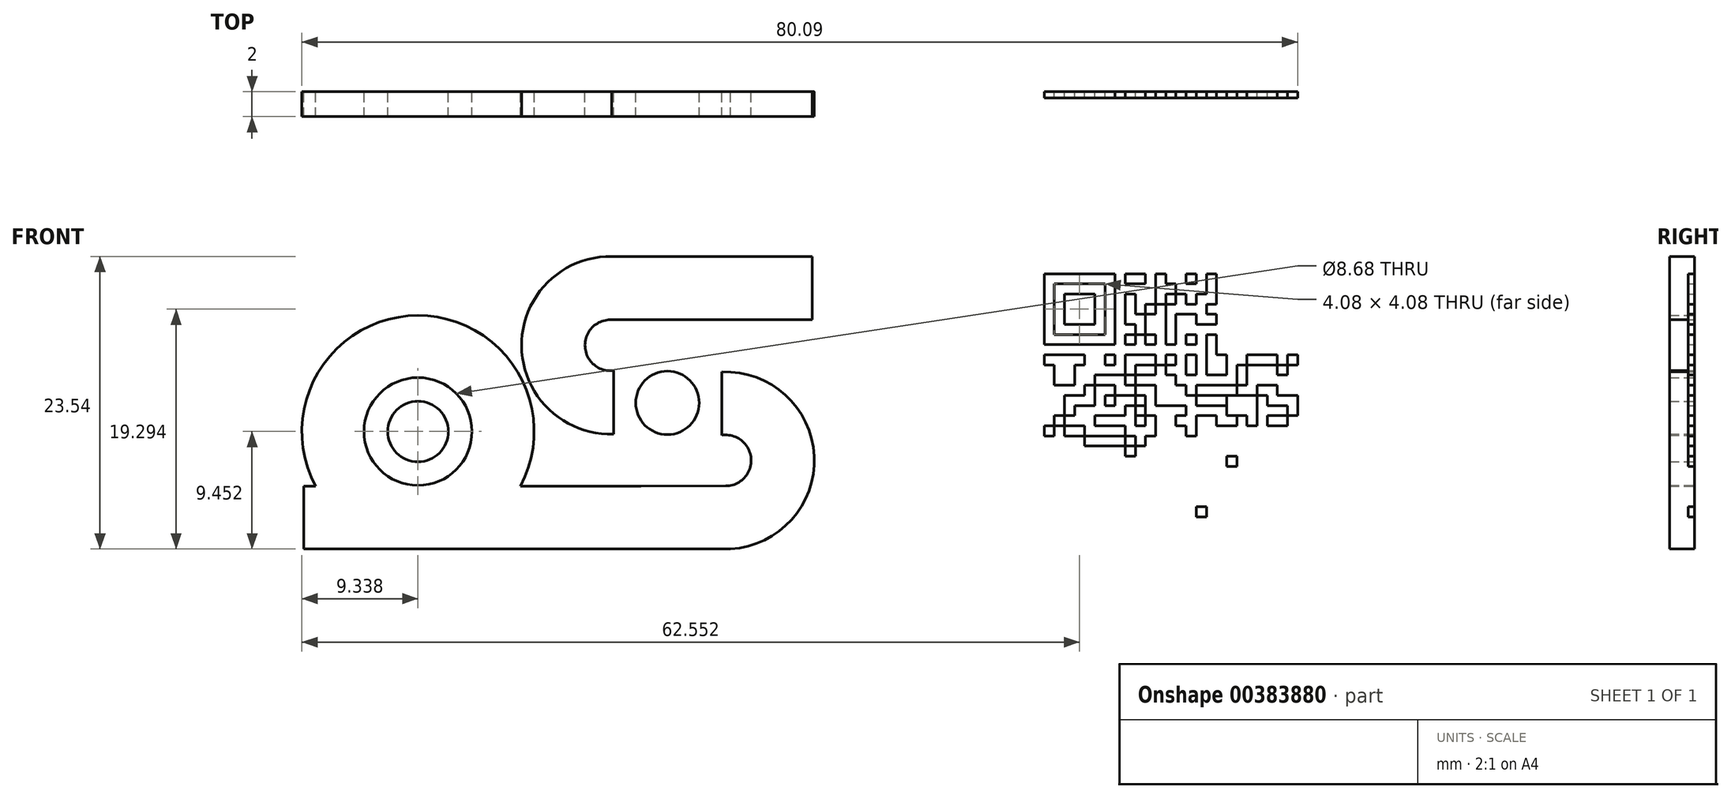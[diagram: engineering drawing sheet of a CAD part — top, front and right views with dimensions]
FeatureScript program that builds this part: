
annotation { "Feature Type Name" : "Feature", "Feature Type Description" : "" }
export const myFeature = defineFeature(function(context is Context, id is Id, definition is map)
    precondition{}
    {
        {
            var Q0;
            Q0=qCreatedBy(makeId("Front.planeOp"),FACE);
            var sketch = newSketch(context, id + "F0", { "sketchPlane" : qUnion([Q0])});
            skCircle(sketch, "E0", {"center": v(-32.73, 10.63) * mm, "radius": 2.44 * mm});
            skCircle(sketch, "E1.0", {"center": v(-32.73, 10.63) * mm, "radius": 4.34 * mm});
            skArc(sketch, "E2.0", {"start": v(-24.49, 6.24) * mm, "mid": v(-32.74, 19.97) * mm, "end": v(-40.97, 6.22) * mm});
            skLineSegment(sketch, "E3", {"start": v(-40.97, 6.22) * mm, "end": v(-41.91, 6.22) * mm});
            skLineSegment(sketch, "E4", {"start": v(-41.91, 6.22) * mm, "end": v(-41.91, 1.18) * mm});
            skLineSegment(sketch, "E5", {"start": v(-41.91, 1.18) * mm, "end": v(-7.6, 1.18) * mm});
            skArc(sketch, "E6", {"start": v(-7.98, 6.25) * mm, "mid": v(-5.94, 8.46) * mm, "end": v(-8.3, 10.33) * mm});
            skCircle(sketch, "E7", {"center": v(-12.67, 12.94) * mm, "radius": 2.55 * mm});
            skLineSegment(sketch, "E8", {"start": v(-8.3, 10.33) * mm, "end": v(-8.3, 15.43) * mm});
            skArc(sketch, "E9.0", {"start": v(-8.37, 1.18) * mm, "mid": v(-0.86, 8.27) * mm, "end": v(-8.3, 15.43) * mm});
            skLineSegment(sketch, "E10", {"start": v(-24.49, 6.24) * mm, "end": v(-14.81, 6.24) * mm});
            skLineSegment(sketch, "E11", {"start": v(-14.81, 6.24) * mm, "end": v(-7.98, 6.25) * mm});
            skArc(sketch, "E12", {"start": v(-17.25, 19.62) * mm, "mid": v(-19.3, 17.45) * mm, "end": v(-17, 15.54) * mm});
            skArc(sketch, "E13.0", {"start": v(-17.16, 24.72) * mm, "mid": v(-24.4, 17.5) * mm, "end": v(-17, 10.43) * mm});
            skLineSegment(sketch, "E14", {"start": v(-17, 15.54) * mm, "end": v(-17, 10.43) * mm});
            skLineSegment(sketch, "E15", {"start": v(-17.16, 24.72) * mm, "end": v(-1.01, 24.72) * mm});
            skLineSegment(sketch, "E16", {"start": v(-1.01, 24.72) * mm, "end": v(-1.01, 19.62) * mm});
            skLineSegment(sketch, "E17", {"start": v(-1.01, 19.62) * mm, "end": v(-17.25, 19.62) * mm});
            skSolve(sketch);
        }
        {
            var Q0;
            Q0=makeQuery(id+"F0.imprint","IMPRINT",FACE,{"disambiguationData":[TD([[makeQuery(id+"F0.imprint","IMPRINT",EDGE,{"derivedFrom":sQuery(id+"F0.wireOp",EDGE,"E1.0")}),-1.0]])]});
            var Q1;
            Q1=makeQuery(id+"F0.imprint","IMPRINT",FACE,{"disambiguationData":[TD([[makeQuery(id+"F0.imprint","IMPRINT",EDGE,{"derivedFrom":sQuery(id+"F0.wireOp",EDGE,"E0")}),1.0]])]});
            var Q2;
            Q2=makeQuery(id+"F0.imprint","IMPRINT",FACE,{"disambiguationData":[TD([[makeQuery(id+"F0.imprint","IMPRINT",EDGE,{"derivedFrom":sQuery(id+"F0.wireOp",EDGE,"E12")}),-1.0]])]});
            var Q3;
            Q3=makeQuery(id+"F0.imprint","IMPRINT",FACE,{"disambiguationData":[TD([[makeQuery(id+"F0.imprint","IMPRINT",EDGE,{"derivedFrom":sQuery(id+"F0.wireOp",EDGE,"E7")}),1.0]])]});
            extrude(context, id + "F1", {"entities" : qUnion([Q0, Q1, Q2, Q3]), "depth" : 2 * mm});
        }
        {
            var Q0;
            Q0=qCreatedBy(makeId("Front.planeOp"),FACE);
            var sketch = newSketch(context, id + "F2", { "sketchPlane" : qUnion([Q0])});
            skLineSegment(sketch, "E18", {"start": v(79.5, 79.25) * mm, "end": v(79.5, -80.75) * mm});
            skLineSegment(sketch, "E19", {"start": v(79.5, -80.75) * mm, "end": v(-80.5, -80.75) * mm});
            skLineSegment(sketch, "E20", {"start": v(80.5, 80.75) * mm, "end": v(80.5, -79.25) * mm});
            skLineSegment(sketch, "E21", {"start": v(80.5, -79.25) * mm, "end": v(-79.5, -79.25) * mm});
            skLineSegment(sketch, "E22", {"start": v(17.63, 23.33) * mm, "end": v(17.63, 22.51) * mm});
            skLineSegment(sketch, "E23", {"start": v(17.63, 22.51) * mm, "end": v(17.63, 21.7) * mm});
            skLineSegment(sketch, "E24", {"start": v(17.63, 21.7) * mm, "end": v(17.63, 20.88) * mm});
            skLineSegment(sketch, "E25", {"start": v(17.63, 20.88) * mm, "end": v(17.63, 20.07) * mm});
            skLineSegment(sketch, "E26", {"start": v(17.63, 20.07) * mm, "end": v(17.63, 19.25) * mm});
            skLineSegment(sketch, "E27", {"start": v(17.63, 19.25) * mm, "end": v(17.63, 18.44) * mm});
            skLineSegment(sketch, "E28", {"start": v(17.63, 18.44) * mm, "end": v(17.63, 17.62) * mm});
            skLineSegment(sketch, "E29", {"start": v(17.63, 17.62) * mm, "end": v(18.44, 17.62) * mm});
            skLineSegment(sketch, "E30", {"start": v(18.44, 17.62) * mm, "end": v(19.26, 17.62) * mm});
            skLineSegment(sketch, "E31", {"start": v(19.26, 17.62) * mm, "end": v(20.07, 17.62) * mm});
            skLineSegment(sketch, "E32", {"start": v(20.07, 17.62) * mm, "end": v(20.9, 17.62) * mm});
            skLineSegment(sketch, "E33", {"start": v(20.9, 17.62) * mm, "end": v(21.7, 17.62) * mm});
            skLineSegment(sketch, "E34", {"start": v(21.7, 17.62) * mm, "end": v(22.52, 17.62) * mm});
            skLineSegment(sketch, "E35", {"start": v(22.52, 17.62) * mm, "end": v(23.34, 17.62) * mm});
            skLineSegment(sketch, "E36", {"start": v(23.34, 17.62) * mm, "end": v(23.34, 18.44) * mm});
            skLineSegment(sketch, "E37", {"start": v(23.34, 18.44) * mm, "end": v(23.34, 19.25) * mm});
            skLineSegment(sketch, "E38", {"start": v(23.34, 19.25) * mm, "end": v(23.34, 20.07) * mm});
            skLineSegment(sketch, "E39", {"start": v(23.34, 20.07) * mm, "end": v(23.34, 20.88) * mm});
            skLineSegment(sketch, "E40", {"start": v(23.34, 20.88) * mm, "end": v(23.34, 21.7) * mm});
            skLineSegment(sketch, "E41", {"start": v(23.34, 21.7) * mm, "end": v(23.34, 22.51) * mm});
            skLineSegment(sketch, "E42", {"start": v(23.34, 22.51) * mm, "end": v(23.34, 23.33) * mm});
            skLineSegment(sketch, "E43", {"start": v(23.34, 23.33) * mm, "end": v(22.52, 23.33) * mm});
            skLineSegment(sketch, "E44", {"start": v(22.52, 23.33) * mm, "end": v(21.7, 23.33) * mm});
            skLineSegment(sketch, "E45", {"start": v(21.7, 23.33) * mm, "end": v(20.9, 23.33) * mm});
            skLineSegment(sketch, "E46", {"start": v(20.9, 23.33) * mm, "end": v(20.07, 23.33) * mm});
            skLineSegment(sketch, "E47", {"start": v(20.07, 23.33) * mm, "end": v(19.26, 23.33) * mm});
            skLineSegment(sketch, "E48", {"start": v(19.26, 23.33) * mm, "end": v(18.44, 23.33) * mm});
            skLineSegment(sketch, "E49", {"start": v(18.44, 23.33) * mm, "end": v(17.63, 23.33) * mm});
            skLineSegment(sketch, "E50", {"start": v(24.15, 23.33) * mm, "end": v(24.15, 22.51) * mm});
            skLineSegment(sketch, "E51", {"start": v(24.15, 22.51) * mm, "end": v(24.97, 22.51) * mm});
            skLineSegment(sketch, "E52", {"start": v(24.97, 22.51) * mm, "end": v(25.78, 22.51) * mm});
            skLineSegment(sketch, "E53", {"start": v(25.78, 22.51) * mm, "end": v(25.78, 23.33) * mm});
            skLineSegment(sketch, "E54", {"start": v(25.78, 23.33) * mm, "end": v(24.97, 23.33) * mm});
            skLineSegment(sketch, "E55", {"start": v(24.97, 23.33) * mm, "end": v(24.15, 23.33) * mm});
            skLineSegment(sketch, "E56", {"start": v(26.6, 23.33) * mm, "end": v(26.6, 22.51) * mm});
            skLineSegment(sketch, "E57", {"start": v(26.6, 22.51) * mm, "end": v(26.6, 21.7) * mm});
            skLineSegment(sketch, "E58", {"start": v(26.6, 21.7) * mm, "end": v(26.6, 20.88) * mm});
            skLineSegment(sketch, "E59", {"start": v(26.6, 20.88) * mm, "end": v(27.42, 20.88) * mm});
            skLineSegment(sketch, "E60", {"start": v(27.42, 20.88) * mm, "end": v(27.42, 21.7) * mm});
            skLineSegment(sketch, "E61", {"start": v(27.42, 21.7) * mm, "end": v(28.23, 21.7) * mm});
            skLineSegment(sketch, "E62", {"start": v(28.23, 21.7) * mm, "end": v(28.23, 22.51) * mm});
            skLineSegment(sketch, "E63", {"start": v(28.23, 22.51) * mm, "end": v(27.42, 22.51) * mm});
            skLineSegment(sketch, "E64", {"start": v(27.42, 22.51) * mm, "end": v(27.42, 23.33) * mm});
            skLineSegment(sketch, "E65", {"start": v(27.42, 23.33) * mm, "end": v(26.6, 23.33) * mm});
            skLineSegment(sketch, "E66", {"start": v(28.23, 21.7) * mm, "end": v(28.23, 20.88) * mm});
            skLineSegment(sketch, "E67", {"start": v(28.23, 20.88) * mm, "end": v(27.42, 20.88) * mm});
            skLineSegment(sketch, "E68", {"start": v(27.42, 20.88) * mm, "end": v(27.42, 20.07) * mm});
            skLineSegment(sketch, "E69", {"start": v(27.42, 20.07) * mm, "end": v(27.42, 19.25) * mm});
            skLineSegment(sketch, "E70", {"start": v(27.42, 19.25) * mm, "end": v(27.42, 18.44) * mm});
            skLineSegment(sketch, "E71", {"start": v(27.42, 18.44) * mm, "end": v(27.42, 17.62) * mm});
            skLineSegment(sketch, "E72", {"start": v(27.42, 17.62) * mm, "end": v(28.23, 17.62) * mm});
            skLineSegment(sketch, "E73", {"start": v(28.23, 17.62) * mm, "end": v(28.23, 18.44) * mm});
            skLineSegment(sketch, "E74", {"start": v(28.23, 18.44) * mm, "end": v(28.23, 19.25) * mm});
            skLineSegment(sketch, "E75", {"start": v(28.23, 19.25) * mm, "end": v(28.23, 20.07) * mm});
            skLineSegment(sketch, "E76", {"start": v(28.23, 20.07) * mm, "end": v(29.05, 20.07) * mm});
            skLineSegment(sketch, "E77", {"start": v(29.05, 20.07) * mm, "end": v(29.86, 20.07) * mm});
            skLineSegment(sketch, "E78", {"start": v(29.86, 20.07) * mm, "end": v(29.86, 19.25) * mm});
            skLineSegment(sketch, "E79", {"start": v(29.86, 19.25) * mm, "end": v(30.68, 19.25) * mm});
            skLineSegment(sketch, "E80", {"start": v(30.68, 19.25) * mm, "end": v(31.5, 19.25) * mm});
            skLineSegment(sketch, "E81", {"start": v(31.5, 19.25) * mm, "end": v(31.5, 20.07) * mm});
            skLineSegment(sketch, "E82", {"start": v(31.5, 20.07) * mm, "end": v(30.68, 20.07) * mm});
            skLineSegment(sketch, "E83", {"start": v(30.68, 20.07) * mm, "end": v(30.68, 20.88) * mm});
            skLineSegment(sketch, "E84", {"start": v(30.68, 20.88) * mm, "end": v(31.5, 20.88) * mm});
            skLineSegment(sketch, "E85", {"start": v(31.5, 20.88) * mm, "end": v(31.5, 21.7) * mm});
            skLineSegment(sketch, "E86", {"start": v(31.5, 21.7) * mm, "end": v(31.5, 22.51) * mm});
            skLineSegment(sketch, "E87", {"start": v(31.5, 22.51) * mm, "end": v(31.5, 23.33) * mm});
            skLineSegment(sketch, "E88", {"start": v(31.5, 23.33) * mm, "end": v(30.68, 23.33) * mm});
            skLineSegment(sketch, "E89", {"start": v(30.68, 23.33) * mm, "end": v(30.68, 22.51) * mm});
            skLineSegment(sketch, "E90", {"start": v(30.68, 22.51) * mm, "end": v(30.68, 21.7) * mm});
            skLineSegment(sketch, "E91", {"start": v(30.68, 21.7) * mm, "end": v(29.86, 21.7) * mm});
            skLineSegment(sketch, "E92", {"start": v(29.86, 21.7) * mm, "end": v(29.86, 20.88) * mm});
            skLineSegment(sketch, "E93", {"start": v(29.86, 20.88) * mm, "end": v(29.05, 20.88) * mm});
            skLineSegment(sketch, "E94", {"start": v(29.05, 20.88) * mm, "end": v(29.05, 21.7) * mm});
            skLineSegment(sketch, "E95", {"start": v(29.05, 21.7) * mm, "end": v(28.23, 21.7) * mm});
            skLineSegment(sketch, "E96", {"start": v(26.6, 20.88) * mm, "end": v(25.78, 20.88) * mm});
            skLineSegment(sketch, "E97", {"start": v(25.78, 20.88) * mm, "end": v(25.78, 20.07) * mm});
            skLineSegment(sketch, "E98", {"start": v(25.78, 20.07) * mm, "end": v(26.6, 20.07) * mm});
            skLineSegment(sketch, "E99", {"start": v(26.6, 20.07) * mm, "end": v(26.6, 20.88) * mm});
            skLineSegment(sketch, "E100", {"start": v(25.78, 20.07) * mm, "end": v(24.97, 20.07) * mm});
            skLineSegment(sketch, "E101", {"start": v(24.97, 20.07) * mm, "end": v(24.97, 20.88) * mm});
            skLineSegment(sketch, "E102", {"start": v(24.97, 20.88) * mm, "end": v(24.97, 21.7) * mm});
            skLineSegment(sketch, "E103", {"start": v(24.97, 21.7) * mm, "end": v(24.15, 21.7) * mm});
            skLineSegment(sketch, "E104", {"start": v(24.15, 21.7) * mm, "end": v(24.15, 20.88) * mm});
            skLineSegment(sketch, "E105", {"start": v(24.15, 20.88) * mm, "end": v(24.15, 20.07) * mm});
            skLineSegment(sketch, "E106", {"start": v(24.15, 20.07) * mm, "end": v(24.15, 19.25) * mm});
            skLineSegment(sketch, "E107", {"start": v(24.15, 19.25) * mm, "end": v(24.97, 19.25) * mm});
            skLineSegment(sketch, "E108", {"start": v(24.97, 19.25) * mm, "end": v(24.97, 18.44) * mm});
            skLineSegment(sketch, "E109", {"start": v(24.97, 18.44) * mm, "end": v(25.78, 18.44) * mm});
            skLineSegment(sketch, "E110", {"start": v(25.78, 18.44) * mm, "end": v(25.78, 19.25) * mm});
            skLineSegment(sketch, "E111", {"start": v(25.78, 19.25) * mm, "end": v(25.78, 20.07) * mm});
            skLineSegment(sketch, "E112", {"start": v(25.78, 18.44) * mm, "end": v(25.78, 17.62) * mm});
            skLineSegment(sketch, "E113", {"start": v(25.78, 17.62) * mm, "end": v(26.6, 17.62) * mm});
            skLineSegment(sketch, "E114", {"start": v(26.6, 17.62) * mm, "end": v(26.6, 18.44) * mm});
            skLineSegment(sketch, "E115", {"start": v(26.6, 18.44) * mm, "end": v(25.78, 18.44) * mm});
            skLineSegment(sketch, "E116", {"start": v(24.97, 18.44) * mm, "end": v(24.15, 18.44) * mm});
            skLineSegment(sketch, "E117", {"start": v(24.15, 18.44) * mm, "end": v(24.15, 17.62) * mm});
            skLineSegment(sketch, "E118", {"start": v(24.15, 17.62) * mm, "end": v(24.97, 17.62) * mm});
            skLineSegment(sketch, "E119", {"start": v(24.97, 17.62) * mm, "end": v(24.97, 18.44) * mm});
            skLineSegment(sketch, "E120", {"start": v(29.05, 23.33) * mm, "end": v(29.05, 22.51) * mm});
            skLineSegment(sketch, "E121", {"start": v(29.05, 22.51) * mm, "end": v(29.86, 22.51) * mm});
            skLineSegment(sketch, "E122", {"start": v(29.86, 22.51) * mm, "end": v(29.86, 23.33) * mm});
            skLineSegment(sketch, "E123", {"start": v(29.86, 23.33) * mm, "end": v(29.05, 23.33) * mm});
            skLineSegment(sketch, "E124", {"start": v(32.3, 23.33) * mm, "end": v(32.3, 22.51) * mm});
            skLineSegment(sketch, "E125", {"start": v(32.3, 22.51) * mm, "end": v(32.3, 21.7) * mm});
            skLineSegment(sketch, "E126", {"start": v(32.3, 21.7) * mm, "end": v(32.3, 20.88) * mm});
            skLineSegment(sketch, "E127", {"start": v(32.3, 20.88) * mm, "end": v(32.3, 20.07) * mm});
            skLineSegment(sketch, "E128", {"start": v(32.3, 20.07) * mm, "end": v(32.3, 19.25) * mm});
            skLineSegment(sketch, "E129", {"start": v(32.3, 19.25) * mm, "end": v(32.3, 18.44) * mm});
            skLineSegment(sketch, "E130", {"start": v(32.3, 18.44) * mm, "end": v(32.3, 17.62) * mm});
            skLineSegment(sketch, "E131", {"start": v(32.3, 17.62) * mm, "end": v(33.12, 17.62) * mm});
            skLineSegment(sketch, "E132", {"start": v(33.12, 17.62) * mm, "end": v(33.94, 17.62) * mm});
            skLineSegment(sketch, "E133", {"start": v(33.94, 17.62) * mm, "end": v(34.76, 17.62) * mm});
            skLineSegment(sketch, "E134", {"start": v(34.76, 17.62) * mm, "end": v(35.57, 17.62) * mm});
            skLineSegment(sketch, "E135", {"start": v(35.57, 17.62) * mm, "end": v(36.39, 17.62) * mm});
            skLineSegment(sketch, "E136", {"start": v(36.39, 17.62) * mm, "end": v(37.2, 17.62) * mm});
            skLineSegment(sketch, "E137", {"start": v(37.2, 17.62) * mm, "end": v(38.02, 17.62) * mm});
            skLineSegment(sketch, "E138", {"start": v(38.02, 17.62) * mm, "end": v(38.02, 18.44) * mm});
            skLineSegment(sketch, "E139", {"start": v(38.02, 18.44) * mm, "end": v(38.02, 19.25) * mm});
            skLineSegment(sketch, "E140", {"start": v(38.02, 19.25) * mm, "end": v(38.02, 20.07) * mm});
            skLineSegment(sketch, "E141", {"start": v(38.02, 20.07) * mm, "end": v(38.02, 20.88) * mm});
            skLineSegment(sketch, "E142", {"start": v(38.02, 20.88) * mm, "end": v(38.02, 21.7) * mm});
            skLineSegment(sketch, "E143", {"start": v(38.02, 21.7) * mm, "end": v(38.02, 22.51) * mm});
            skLineSegment(sketch, "E144", {"start": v(38.02, 22.51) * mm, "end": v(38.02, 23.33) * mm});
            skLineSegment(sketch, "E145", {"start": v(38.02, 23.33) * mm, "end": v(37.2, 23.33) * mm});
            skLineSegment(sketch, "E146", {"start": v(37.2, 23.33) * mm, "end": v(36.39, 23.33) * mm});
            skLineSegment(sketch, "E147", {"start": v(36.39, 23.33) * mm, "end": v(35.57, 23.33) * mm});
            skLineSegment(sketch, "E148", {"start": v(35.57, 23.33) * mm, "end": v(34.76, 23.33) * mm});
            skLineSegment(sketch, "E149", {"start": v(34.76, 23.33) * mm, "end": v(33.94, 23.33) * mm});
            skLineSegment(sketch, "E150", {"start": v(33.94, 23.33) * mm, "end": v(33.12, 23.33) * mm});
            skLineSegment(sketch, "E151", {"start": v(33.12, 23.33) * mm, "end": v(32.3, 23.33) * mm});
            skLineSegment(sketch, "E152", {"start": v(18.44, 22.51) * mm, "end": v(19.26, 22.51) * mm});
            skLineSegment(sketch, "E153", {"start": v(19.26, 22.51) * mm, "end": v(20.07, 22.51) * mm});
            skLineSegment(sketch, "E154", {"start": v(20.07, 22.51) * mm, "end": v(20.9, 22.51) * mm});
            skLineSegment(sketch, "E155", {"start": v(20.9, 22.51) * mm, "end": v(21.7, 22.51) * mm});
            skLineSegment(sketch, "E156", {"start": v(21.7, 22.51) * mm, "end": v(22.52, 22.51) * mm});
            skLineSegment(sketch, "E157", {"start": v(22.52, 22.51) * mm, "end": v(22.52, 21.7) * mm});
            skLineSegment(sketch, "E158", {"start": v(22.52, 21.7) * mm, "end": v(22.52, 20.88) * mm});
            skLineSegment(sketch, "E159", {"start": v(22.52, 20.88) * mm, "end": v(22.52, 20.07) * mm});
            skLineSegment(sketch, "E160", {"start": v(22.52, 20.07) * mm, "end": v(22.52, 19.25) * mm});
            skLineSegment(sketch, "E161", {"start": v(22.52, 19.25) * mm, "end": v(22.52, 18.44) * mm});
            skLineSegment(sketch, "E162", {"start": v(22.52, 18.44) * mm, "end": v(21.7, 18.44) * mm});
            skLineSegment(sketch, "E163", {"start": v(21.7, 18.44) * mm, "end": v(20.9, 18.44) * mm});
            skLineSegment(sketch, "E164", {"start": v(20.9, 18.44) * mm, "end": v(20.07, 18.44) * mm});
            skLineSegment(sketch, "E165", {"start": v(20.07, 18.44) * mm, "end": v(19.26, 18.44) * mm});
            skLineSegment(sketch, "E166", {"start": v(19.26, 18.44) * mm, "end": v(18.44, 18.44) * mm});
            skLineSegment(sketch, "E167", {"start": v(18.44, 18.44) * mm, "end": v(18.44, 19.25) * mm});
            skLineSegment(sketch, "E168", {"start": v(18.44, 19.25) * mm, "end": v(18.44, 20.07) * mm});
            skLineSegment(sketch, "E169", {"start": v(18.44, 20.07) * mm, "end": v(18.44, 20.88) * mm});
            skLineSegment(sketch, "E170", {"start": v(18.44, 20.88) * mm, "end": v(18.44, 21.7) * mm});
            skLineSegment(sketch, "E171", {"start": v(18.44, 21.7) * mm, "end": v(18.44, 22.51) * mm});
            skLineSegment(sketch, "E172", {"start": v(33.12, 22.51) * mm, "end": v(33.94, 22.51) * mm});
            skLineSegment(sketch, "E173", {"start": v(33.94, 22.51) * mm, "end": v(34.76, 22.51) * mm});
            skLineSegment(sketch, "E174", {"start": v(34.76, 22.51) * mm, "end": v(35.57, 22.51) * mm});
            skLineSegment(sketch, "E175", {"start": v(35.57, 22.51) * mm, "end": v(36.39, 22.51) * mm});
            skLineSegment(sketch, "E176", {"start": v(36.39, 22.51) * mm, "end": v(37.2, 22.51) * mm});
            skLineSegment(sketch, "E177", {"start": v(37.2, 22.51) * mm, "end": v(37.2, 21.7) * mm});
            skLineSegment(sketch, "E178", {"start": v(37.2, 21.7) * mm, "end": v(37.2, 20.88) * mm});
            skLineSegment(sketch, "E179", {"start": v(37.2, 20.88) * mm, "end": v(37.2, 20.07) * mm});
            skLineSegment(sketch, "E180", {"start": v(37.2, 20.07) * mm, "end": v(37.2, 19.25) * mm});
            skLineSegment(sketch, "E181", {"start": v(37.2, 19.25) * mm, "end": v(37.2, 18.44) * mm});
            skLineSegment(sketch, "E182", {"start": v(37.2, 18.44) * mm, "end": v(36.39, 18.44) * mm});
            skLineSegment(sketch, "E183", {"start": v(36.39, 18.44) * mm, "end": v(35.57, 18.44) * mm});
            skLineSegment(sketch, "E184", {"start": v(35.57, 18.44) * mm, "end": v(34.76, 18.44) * mm});
            skLineSegment(sketch, "E185", {"start": v(34.76, 18.44) * mm, "end": v(33.94, 18.44) * mm});
            skLineSegment(sketch, "E186", {"start": v(33.94, 18.44) * mm, "end": v(33.12, 18.44) * mm});
            skLineSegment(sketch, "E187", {"start": v(33.12, 18.44) * mm, "end": v(33.12, 19.25) * mm});
            skLineSegment(sketch, "E188", {"start": v(33.12, 19.25) * mm, "end": v(33.12, 20.07) * mm});
            skLineSegment(sketch, "E189", {"start": v(33.12, 20.07) * mm, "end": v(33.12, 20.88) * mm});
            skLineSegment(sketch, "E190", {"start": v(33.12, 20.88) * mm, "end": v(33.12, 21.7) * mm});
            skLineSegment(sketch, "E191", {"start": v(33.12, 21.7) * mm, "end": v(33.12, 22.51) * mm});
            skLineSegment(sketch, "E192", {"start": v(19.26, 21.7) * mm, "end": v(19.26, 20.88) * mm});
            skLineSegment(sketch, "E193", {"start": v(19.26, 20.88) * mm, "end": v(19.26, 20.07) * mm});
            skLineSegment(sketch, "E194", {"start": v(19.26, 20.07) * mm, "end": v(19.26, 19.25) * mm});
            skLineSegment(sketch, "E195", {"start": v(19.26, 19.25) * mm, "end": v(20.07, 19.25) * mm});
            skLineSegment(sketch, "E196", {"start": v(20.07, 19.25) * mm, "end": v(20.9, 19.25) * mm});
            skLineSegment(sketch, "E197", {"start": v(20.9, 19.25) * mm, "end": v(21.7, 19.25) * mm});
            skLineSegment(sketch, "E198", {"start": v(21.7, 19.25) * mm, "end": v(21.7, 20.07) * mm});
            skLineSegment(sketch, "E199", {"start": v(21.7, 20.07) * mm, "end": v(21.7, 20.88) * mm});
            skLineSegment(sketch, "E200", {"start": v(21.7, 20.88) * mm, "end": v(21.7, 21.7) * mm});
            skLineSegment(sketch, "E201", {"start": v(21.7, 21.7) * mm, "end": v(20.9, 21.7) * mm});
            skLineSegment(sketch, "E202", {"start": v(20.9, 21.7) * mm, "end": v(20.07, 21.7) * mm});
            skLineSegment(sketch, "E203", {"start": v(20.07, 21.7) * mm, "end": v(19.26, 21.7) * mm});
            skLineSegment(sketch, "E204", {"start": v(33.94, 21.7) * mm, "end": v(33.94, 20.88) * mm});
            skLineSegment(sketch, "E205", {"start": v(33.94, 20.88) * mm, "end": v(33.94, 20.07) * mm});
            skLineSegment(sketch, "E206", {"start": v(33.94, 20.07) * mm, "end": v(33.94, 19.25) * mm});
            skLineSegment(sketch, "E207", {"start": v(33.94, 19.25) * mm, "end": v(34.76, 19.25) * mm});
            skLineSegment(sketch, "E208", {"start": v(34.76, 19.25) * mm, "end": v(35.57, 19.25) * mm});
            skLineSegment(sketch, "E209", {"start": v(35.57, 19.25) * mm, "end": v(36.39, 19.25) * mm});
            skLineSegment(sketch, "E210", {"start": v(36.39, 19.25) * mm, "end": v(36.39, 20.07) * mm});
            skLineSegment(sketch, "E211", {"start": v(36.39, 20.07) * mm, "end": v(36.39, 20.88) * mm});
            skLineSegment(sketch, "E212", {"start": v(36.39, 20.88) * mm, "end": v(36.39, 21.7) * mm});
            skLineSegment(sketch, "E213", {"start": v(36.39, 21.7) * mm, "end": v(35.57, 21.7) * mm});
            skLineSegment(sketch, "E214", {"start": v(35.57, 21.7) * mm, "end": v(34.76, 21.7) * mm});
            skLineSegment(sketch, "E215", {"start": v(34.76, 21.7) * mm, "end": v(33.94, 21.7) * mm});
            skLineSegment(sketch, "E216", {"start": v(29.05, 18.44) * mm, "end": v(29.05, 17.62) * mm});
            skLineSegment(sketch, "E217", {"start": v(29.05, 17.62) * mm, "end": v(29.86, 17.62) * mm});
            skLineSegment(sketch, "E218", {"start": v(29.86, 17.62) * mm, "end": v(29.86, 18.44) * mm});
            skLineSegment(sketch, "E219", {"start": v(29.86, 18.44) * mm, "end": v(29.05, 18.44) * mm});
            skLineSegment(sketch, "E220", {"start": v(30.68, 18.44) * mm, "end": v(30.68, 17.62) * mm});
            skLineSegment(sketch, "E221", {"start": v(30.68, 17.62) * mm, "end": v(30.68, 16.8) * mm});
            skLineSegment(sketch, "E222", {"start": v(30.68, 16.8) * mm, "end": v(30.68, 15.99) * mm});
            skLineSegment(sketch, "E223", {"start": v(30.68, 15.99) * mm, "end": v(30.68, 15.17) * mm});
            skLineSegment(sketch, "E224", {"start": v(30.68, 15.17) * mm, "end": v(31.5, 15.17) * mm});
            skLineSegment(sketch, "E225", {"start": v(31.5, 15.17) * mm, "end": v(32.3, 15.17) * mm});
            skLineSegment(sketch, "E226", {"start": v(32.3, 15.17) * mm, "end": v(32.3, 15.99) * mm});
            skLineSegment(sketch, "E227", {"start": v(32.3, 15.99) * mm, "end": v(32.3, 16.8) * mm});
            skLineSegment(sketch, "E228", {"start": v(32.3, 16.8) * mm, "end": v(31.5, 16.8) * mm});
            skLineSegment(sketch, "E229", {"start": v(31.5, 16.8) * mm, "end": v(31.5, 17.62) * mm});
            skLineSegment(sketch, "E230", {"start": v(31.5, 17.62) * mm, "end": v(31.5, 18.44) * mm});
            skLineSegment(sketch, "E231", {"start": v(31.5, 18.44) * mm, "end": v(30.68, 18.44) * mm});
            skLineSegment(sketch, "E232", {"start": v(17.63, 16.8) * mm, "end": v(17.63, 15.99) * mm});
            skLineSegment(sketch, "E233", {"start": v(17.63, 15.99) * mm, "end": v(18.44, 15.99) * mm});
            skLineSegment(sketch, "E234", {"start": v(18.44, 15.99) * mm, "end": v(18.44, 15.17) * mm});
            skLineSegment(sketch, "E235", {"start": v(18.44, 15.17) * mm, "end": v(18.44, 14.36) * mm});
            skLineSegment(sketch, "E236", {"start": v(18.44, 14.36) * mm, "end": v(19.26, 14.36) * mm});
            skLineSegment(sketch, "E237", {"start": v(19.26, 14.36) * mm, "end": v(20.07, 14.36) * mm});
            skLineSegment(sketch, "E238", {"start": v(20.07, 14.36) * mm, "end": v(20.07, 15.17) * mm});
            skLineSegment(sketch, "E239", {"start": v(20.07, 15.17) * mm, "end": v(20.07, 15.99) * mm});
            skLineSegment(sketch, "E240", {"start": v(20.07, 15.99) * mm, "end": v(20.9, 15.99) * mm});
            skLineSegment(sketch, "E241", {"start": v(20.9, 15.99) * mm, "end": v(20.9, 16.8) * mm});
            skLineSegment(sketch, "E242", {"start": v(20.9, 16.8) * mm, "end": v(20.07, 16.8) * mm});
            skLineSegment(sketch, "E243", {"start": v(20.07, 16.8) * mm, "end": v(19.26, 16.8) * mm});
            skLineSegment(sketch, "E244", {"start": v(19.26, 16.8) * mm, "end": v(18.44, 16.8) * mm});
            skLineSegment(sketch, "E245", {"start": v(18.44, 16.8) * mm, "end": v(17.63, 16.8) * mm});
            skLineSegment(sketch, "E246", {"start": v(22.52, 16.8) * mm, "end": v(22.52, 15.99) * mm});
            skLineSegment(sketch, "E247", {"start": v(22.52, 15.99) * mm, "end": v(23.34, 15.99) * mm});
            skLineSegment(sketch, "E248", {"start": v(23.34, 15.99) * mm, "end": v(23.34, 16.8) * mm});
            skLineSegment(sketch, "E249", {"start": v(23.34, 16.8) * mm, "end": v(22.52, 16.8) * mm});
            skLineSegment(sketch, "E250", {"start": v(24.15, 16.8) * mm, "end": v(24.15, 15.99) * mm});
            skLineSegment(sketch, "E251", {"start": v(24.15, 15.99) * mm, "end": v(24.15, 15.17) * mm});
            skLineSegment(sketch, "E252", {"start": v(24.15, 15.17) * mm, "end": v(24.97, 15.17) * mm});
            skLineSegment(sketch, "E253", {"start": v(24.97, 15.17) * mm, "end": v(24.97, 15.99) * mm});
            skLineSegment(sketch, "E254", {"start": v(24.97, 15.99) * mm, "end": v(25.78, 15.99) * mm});
            skLineSegment(sketch, "E255", {"start": v(25.78, 15.99) * mm, "end": v(26.6, 15.99) * mm});
            skLineSegment(sketch, "E256", {"start": v(26.6, 15.99) * mm, "end": v(26.6, 16.8) * mm});
            skLineSegment(sketch, "E257", {"start": v(26.6, 16.8) * mm, "end": v(25.78, 16.8) * mm});
            skLineSegment(sketch, "E258", {"start": v(25.78, 16.8) * mm, "end": v(24.97, 16.8) * mm});
            skLineSegment(sketch, "E259", {"start": v(24.97, 16.8) * mm, "end": v(24.15, 16.8) * mm});
            skLineSegment(sketch, "E260", {"start": v(26.6, 15.99) * mm, "end": v(26.6, 15.17) * mm});
            skLineSegment(sketch, "E261", {"start": v(26.6, 15.17) * mm, "end": v(25.78, 15.17) * mm});
            skLineSegment(sketch, "E262", {"start": v(25.78, 15.17) * mm, "end": v(24.97, 15.17) * mm});
            skLineSegment(sketch, "E263", {"start": v(24.97, 15.17) * mm, "end": v(24.97, 14.36) * mm});
            skLineSegment(sketch, "E264", {"start": v(24.97, 14.36) * mm, "end": v(25.78, 14.36) * mm});
            skLineSegment(sketch, "E265", {"start": v(25.78, 14.36) * mm, "end": v(26.6, 14.36) * mm});
            skLineSegment(sketch, "E266", {"start": v(26.6, 14.36) * mm, "end": v(26.6, 13.54) * mm});
            skLineSegment(sketch, "E267", {"start": v(26.6, 13.54) * mm, "end": v(26.6, 12.73) * mm});
            skLineSegment(sketch, "E268", {"start": v(26.6, 12.73) * mm, "end": v(27.42, 12.73) * mm});
            skLineSegment(sketch, "E269", {"start": v(27.42, 12.73) * mm, "end": v(28.23, 12.73) * mm});
            skLineSegment(sketch, "E270", {"start": v(28.23, 12.73) * mm, "end": v(29.05, 12.73) * mm});
            skLineSegment(sketch, "E271", {"start": v(29.05, 12.73) * mm, "end": v(29.05, 11.91) * mm});
            skLineSegment(sketch, "E272", {"start": v(29.05, 11.91) * mm, "end": v(28.23, 11.91) * mm});
            skLineSegment(sketch, "E273", {"start": v(28.23, 11.91) * mm, "end": v(28.23, 11.1) * mm});
            skLineSegment(sketch, "E274", {"start": v(28.23, 11.1) * mm, "end": v(29.05, 11.1) * mm});
            skLineSegment(sketch, "E275", {"start": v(29.05, 11.1) * mm, "end": v(29.05, 10.28) * mm});
            skLineSegment(sketch, "E276", {"start": v(29.05, 10.28) * mm, "end": v(29.86, 10.28) * mm});
            skLineSegment(sketch, "E277", {"start": v(29.86, 10.28) * mm, "end": v(29.86, 11.1) * mm});
            skLineSegment(sketch, "E278", {"start": v(29.86, 11.1) * mm, "end": v(29.86, 11.91) * mm});
            skLineSegment(sketch, "E279", {"start": v(29.86, 11.91) * mm, "end": v(30.68, 11.91) * mm});
            skLineSegment(sketch, "E280", {"start": v(30.68, 11.91) * mm, "end": v(31.5, 11.91) * mm});
            skLineSegment(sketch, "E281", {"start": v(31.5, 11.91) * mm, "end": v(31.5, 11.1) * mm});
            skLineSegment(sketch, "E282", {"start": v(31.5, 11.1) * mm, "end": v(32.3, 11.1) * mm});
            skLineSegment(sketch, "E283", {"start": v(32.3, 11.1) * mm, "end": v(33.12, 11.1) * mm});
            skLineSegment(sketch, "E284", {"start": v(33.12, 11.1) * mm, "end": v(33.12, 11.91) * mm});
            skLineSegment(sketch, "E285", {"start": v(33.12, 11.91) * mm, "end": v(33.94, 11.91) * mm});
            skLineSegment(sketch, "E286", {"start": v(33.94, 11.91) * mm, "end": v(33.94, 11.1) * mm});
            skLineSegment(sketch, "E287", {"start": v(33.94, 11.1) * mm, "end": v(34.76, 11.1) * mm});
            skLineSegment(sketch, "E288", {"start": v(34.76, 11.1) * mm, "end": v(34.76, 11.91) * mm});
            skLineSegment(sketch, "E289", {"start": v(34.76, 11.91) * mm, "end": v(34.76, 12.73) * mm});
            skLineSegment(sketch, "E290", {"start": v(34.76, 12.73) * mm, "end": v(34.76, 13.54) * mm});
            skLineSegment(sketch, "E291", {"start": v(34.76, 13.54) * mm, "end": v(33.94, 13.54) * mm});
            skLineSegment(sketch, "E292", {"start": v(33.94, 13.54) * mm, "end": v(33.12, 13.54) * mm});
            skLineSegment(sketch, "E293", {"start": v(33.12, 13.54) * mm, "end": v(33.12, 14.36) * mm});
            skLineSegment(sketch, "E294", {"start": v(33.12, 14.36) * mm, "end": v(32.3, 14.36) * mm});
            skLineSegment(sketch, "E295", {"start": v(32.3, 14.36) * mm, "end": v(31.5, 14.36) * mm});
            skLineSegment(sketch, "E296", {"start": v(31.5, 14.36) * mm, "end": v(30.68, 14.36) * mm});
            skLineSegment(sketch, "E297", {"start": v(30.68, 14.36) * mm, "end": v(29.86, 14.36) * mm});
            skLineSegment(sketch, "E298", {"start": v(29.86, 14.36) * mm, "end": v(29.86, 13.54) * mm});
            skLineSegment(sketch, "E299", {"start": v(29.86, 13.54) * mm, "end": v(30.68, 13.54) * mm});
            skLineSegment(sketch, "E300", {"start": v(30.68, 13.54) * mm, "end": v(31.5, 13.54) * mm});
            skLineSegment(sketch, "E301", {"start": v(31.5, 13.54) * mm, "end": v(32.3, 13.54) * mm});
            skLineSegment(sketch, "E302", {"start": v(32.3, 13.54) * mm, "end": v(32.3, 12.73) * mm});
            skLineSegment(sketch, "E303", {"start": v(32.3, 12.73) * mm, "end": v(31.5, 12.73) * mm});
            skLineSegment(sketch, "E304", {"start": v(31.5, 12.73) * mm, "end": v(30.68, 12.73) * mm});
            skLineSegment(sketch, "E305", {"start": v(30.68, 12.73) * mm, "end": v(29.86, 12.73) * mm});
            skLineSegment(sketch, "E306", {"start": v(29.86, 12.73) * mm, "end": v(29.86, 13.54) * mm});
            skLineSegment(sketch, "E307", {"start": v(29.86, 13.54) * mm, "end": v(29.05, 13.54) * mm});
            skLineSegment(sketch, "E308", {"start": v(29.05, 13.54) * mm, "end": v(29.05, 14.36) * mm});
            skLineSegment(sketch, "E309", {"start": v(29.05, 14.36) * mm, "end": v(28.23, 14.36) * mm});
            skLineSegment(sketch, "E310", {"start": v(28.23, 14.36) * mm, "end": v(28.23, 15.17) * mm});
            skLineSegment(sketch, "E311", {"start": v(28.23, 15.17) * mm, "end": v(27.42, 15.17) * mm});
            skLineSegment(sketch, "E312", {"start": v(27.42, 15.17) * mm, "end": v(27.42, 15.99) * mm});
            skLineSegment(sketch, "E313", {"start": v(27.42, 15.99) * mm, "end": v(26.6, 15.99) * mm});
            skLineSegment(sketch, "E314", {"start": v(27.42, 15.99) * mm, "end": v(28.23, 15.99) * mm});
            skLineSegment(sketch, "E315", {"start": v(28.23, 15.99) * mm, "end": v(28.23, 16.8) * mm});
            skLineSegment(sketch, "E316", {"start": v(28.23, 16.8) * mm, "end": v(27.42, 16.8) * mm});
            skLineSegment(sketch, "E317", {"start": v(27.42, 16.8) * mm, "end": v(27.42, 15.99) * mm});
            skLineSegment(sketch, "E318", {"start": v(33.12, 14.36) * mm, "end": v(33.94, 14.36) * mm});
            skLineSegment(sketch, "E319", {"start": v(33.94, 14.36) * mm, "end": v(33.94, 15.17) * mm});
            skLineSegment(sketch, "E320", {"start": v(33.94, 15.17) * mm, "end": v(33.94, 15.99) * mm});
            skLineSegment(sketch, "E321", {"start": v(33.94, 15.99) * mm, "end": v(33.12, 15.99) * mm});
            skLineSegment(sketch, "E322", {"start": v(33.12, 15.99) * mm, "end": v(33.12, 15.17) * mm});
            skLineSegment(sketch, "E323", {"start": v(33.12, 15.17) * mm, "end": v(33.12, 14.36) * mm});
            skLineSegment(sketch, "E324", {"start": v(33.94, 15.99) * mm, "end": v(34.76, 15.99) * mm});
            skLineSegment(sketch, "E325", {"start": v(34.76, 15.99) * mm, "end": v(35.57, 15.99) * mm});
            skLineSegment(sketch, "E326", {"start": v(35.57, 15.99) * mm, "end": v(36.39, 15.99) * mm});
            skLineSegment(sketch, "E327", {"start": v(36.39, 15.99) * mm, "end": v(36.39, 16.8) * mm});
            skLineSegment(sketch, "E328", {"start": v(36.39, 16.8) * mm, "end": v(35.57, 16.8) * mm});
            skLineSegment(sketch, "E329", {"start": v(35.57, 16.8) * mm, "end": v(34.76, 16.8) * mm});
            skLineSegment(sketch, "E330", {"start": v(34.76, 16.8) * mm, "end": v(33.94, 16.8) * mm});
            skLineSegment(sketch, "E331", {"start": v(33.94, 16.8) * mm, "end": v(33.94, 15.99) * mm});
            skLineSegment(sketch, "E332", {"start": v(36.39, 15.99) * mm, "end": v(36.39, 15.17) * mm});
            skLineSegment(sketch, "E333", {"start": v(36.39, 15.17) * mm, "end": v(37.2, 15.17) * mm});
            skLineSegment(sketch, "E334", {"start": v(37.2, 15.17) * mm, "end": v(37.2, 15.99) * mm});
            skLineSegment(sketch, "E335", {"start": v(37.2, 15.99) * mm, "end": v(36.39, 15.99) * mm});
            skLineSegment(sketch, "E336", {"start": v(37.2, 15.99) * mm, "end": v(38.02, 15.99) * mm});
            skLineSegment(sketch, "E337", {"start": v(38.02, 15.99) * mm, "end": v(38.02, 16.8) * mm});
            skLineSegment(sketch, "E338", {"start": v(38.02, 16.8) * mm, "end": v(37.2, 16.8) * mm});
            skLineSegment(sketch, "E339", {"start": v(37.2, 16.8) * mm, "end": v(37.2, 15.99) * mm});
            skLineSegment(sketch, "E340", {"start": v(34.76, 13.54) * mm, "end": v(35.57, 13.54) * mm});
            skLineSegment(sketch, "E341", {"start": v(35.57, 13.54) * mm, "end": v(35.57, 12.73) * mm});
            skLineSegment(sketch, "E342", {"start": v(35.57, 12.73) * mm, "end": v(36.39, 12.73) * mm});
            skLineSegment(sketch, "E343", {"start": v(36.39, 12.73) * mm, "end": v(37.2, 12.73) * mm});
            skLineSegment(sketch, "E344", {"start": v(37.2, 12.73) * mm, "end": v(37.2, 11.91) * mm});
            skLineSegment(sketch, "E345", {"start": v(37.2, 11.91) * mm, "end": v(38.02, 11.91) * mm});
            skLineSegment(sketch, "E346", {"start": v(38.02, 11.91) * mm, "end": v(38.02, 12.73) * mm});
            skLineSegment(sketch, "E347", {"start": v(38.02, 12.73) * mm, "end": v(38.02, 13.54) * mm});
            skLineSegment(sketch, "E348", {"start": v(38.02, 13.54) * mm, "end": v(37.2, 13.54) * mm});
            skLineSegment(sketch, "E349", {"start": v(37.2, 13.54) * mm, "end": v(36.39, 13.54) * mm});
            skLineSegment(sketch, "E350", {"start": v(36.39, 13.54) * mm, "end": v(36.39, 14.36) * mm});
            skLineSegment(sketch, "E351", {"start": v(36.39, 14.36) * mm, "end": v(35.57, 14.36) * mm});
            skLineSegment(sketch, "E352", {"start": v(35.57, 14.36) * mm, "end": v(34.76, 14.36) * mm});
            skLineSegment(sketch, "E353", {"start": v(34.76, 14.36) * mm, "end": v(34.76, 13.54) * mm});
            skLineSegment(sketch, "E354", {"start": v(37.2, 11.91) * mm, "end": v(36.39, 11.91) * mm});
            skLineSegment(sketch, "E355", {"start": v(36.39, 11.91) * mm, "end": v(35.57, 11.91) * mm});
            skLineSegment(sketch, "E356", {"start": v(35.57, 11.91) * mm, "end": v(35.57, 11.1) * mm});
            skLineSegment(sketch, "E357", {"start": v(35.57, 11.1) * mm, "end": v(36.39, 11.1) * mm});
            skLineSegment(sketch, "E358", {"start": v(36.39, 11.1) * mm, "end": v(37.2, 11.1) * mm});
            skLineSegment(sketch, "E359", {"start": v(37.2, 11.1) * mm, "end": v(37.2, 11.91) * mm});
            skLineSegment(sketch, "E360", {"start": v(37.2, 11.1) * mm, "end": v(37.2, 10.28) * mm});
            skLineSegment(sketch, "E361", {"start": v(37.2, 10.28) * mm, "end": v(36.39, 10.28) * mm});
            skLineSegment(sketch, "E362", {"start": v(36.39, 10.28) * mm, "end": v(35.57, 10.28) * mm});
            skLineSegment(sketch, "E363", {"start": v(35.57, 10.28) * mm, "end": v(35.57, 11.1) * mm});
            skLineSegment(sketch, "E364", {"start": v(35.57, 11.1) * mm, "end": v(34.76, 11.1) * mm});
            skLineSegment(sketch, "E365", {"start": v(34.76, 11.1) * mm, "end": v(34.76, 10.28) * mm});
            skLineSegment(sketch, "E366", {"start": v(34.76, 10.28) * mm, "end": v(33.94, 10.28) * mm});
            skLineSegment(sketch, "E367", {"start": v(33.94, 10.28) * mm, "end": v(33.94, 11.1) * mm});
            skLineSegment(sketch, "E368", {"start": v(33.94, 11.1) * mm, "end": v(33.12, 11.1) * mm});
            skLineSegment(sketch, "E369", {"start": v(33.12, 11.1) * mm, "end": v(33.12, 10.28) * mm});
            skLineSegment(sketch, "E370", {"start": v(33.12, 10.28) * mm, "end": v(32.3, 10.28) * mm});
            skLineSegment(sketch, "E371", {"start": v(32.3, 10.28) * mm, "end": v(31.5, 10.28) * mm});
            skLineSegment(sketch, "E372", {"start": v(31.5, 10.28) * mm, "end": v(31.5, 11.1) * mm});
            skLineSegment(sketch, "E373", {"start": v(31.5, 11.1) * mm, "end": v(30.68, 11.1) * mm});
            skLineSegment(sketch, "E374", {"start": v(30.68, 11.1) * mm, "end": v(30.68, 10.28) * mm});
            skLineSegment(sketch, "E375", {"start": v(30.68, 10.28) * mm, "end": v(29.86, 10.28) * mm});
            skLineSegment(sketch, "E376", {"start": v(29.86, 10.28) * mm, "end": v(29.86, 9.46) * mm});
            skLineSegment(sketch, "E377", {"start": v(29.86, 9.46) * mm, "end": v(30.68, 9.46) * mm});
            skLineSegment(sketch, "E378", {"start": v(30.68, 9.46) * mm, "end": v(30.68, 8.65) * mm});
            skLineSegment(sketch, "E379", {"start": v(30.68, 8.65) * mm, "end": v(30.68, 7.83) * mm});
            skLineSegment(sketch, "E380", {"start": v(30.68, 7.83) * mm, "end": v(29.86, 7.83) * mm});
            skLineSegment(sketch, "E381", {"start": v(29.86, 7.83) * mm, "end": v(29.86, 7.02) * mm});
            skLineSegment(sketch, "E382", {"start": v(29.86, 7.02) * mm, "end": v(30.68, 7.02) * mm});
            skLineSegment(sketch, "E383", {"start": v(30.68, 7.02) * mm, "end": v(30.68, 6.2) * mm});
            skLineSegment(sketch, "E384", {"start": v(30.68, 6.2) * mm, "end": v(29.86, 6.2) * mm});
            skLineSegment(sketch, "E385", {"start": v(29.86, 6.2) * mm, "end": v(29.86, 5.39) * mm});
            skLineSegment(sketch, "E386", {"start": v(29.86, 5.39) * mm, "end": v(30.68, 5.39) * mm});
            skLineSegment(sketch, "E387", {"start": v(30.68, 5.39) * mm, "end": v(31.5, 5.39) * mm});
            skLineSegment(sketch, "E388", {"start": v(31.5, 5.39) * mm, "end": v(32.3, 5.39) * mm});
            skLineSegment(sketch, "E389", {"start": v(32.3, 5.39) * mm, "end": v(32.3, 4.57) * mm});
            skLineSegment(sketch, "E390", {"start": v(32.3, 4.57) * mm, "end": v(33.12, 4.57) * mm});
            skLineSegment(sketch, "E391", {"start": v(33.12, 4.57) * mm, "end": v(33.94, 4.57) * mm});
            skLineSegment(sketch, "E392", {"start": v(33.94, 4.57) * mm, "end": v(33.94, 3.75) * mm});
            skLineSegment(sketch, "E393", {"start": v(33.94, 3.75) * mm, "end": v(33.12, 3.75) * mm});
            skLineSegment(sketch, "E394", {"start": v(33.12, 3.75) * mm, "end": v(32.3, 3.75) * mm});
            skLineSegment(sketch, "E395", {"start": v(32.3, 3.75) * mm, "end": v(32.3, 2.94) * mm});
            skLineSegment(sketch, "E396", {"start": v(32.3, 2.94) * mm, "end": v(33.12, 2.94) * mm});
            skLineSegment(sketch, "E397", {"start": v(33.12, 2.94) * mm, "end": v(33.94, 2.94) * mm});
            skLineSegment(sketch, "E398", {"start": v(33.94, 2.94) * mm, "end": v(34.76, 2.94) * mm});
            skLineSegment(sketch, "E399", {"start": v(34.76, 2.94) * mm, "end": v(35.57, 2.94) * mm});
            skLineSegment(sketch, "E400", {"start": v(35.57, 2.94) * mm, "end": v(36.39, 2.94) * mm});
            skLineSegment(sketch, "E401", {"start": v(36.39, 2.94) * mm, "end": v(37.2, 2.94) * mm});
            skLineSegment(sketch, "E402", {"start": v(37.2, 2.94) * mm, "end": v(38.02, 2.94) * mm});
            skLineSegment(sketch, "E403", {"start": v(38.02, 2.94) * mm, "end": v(38.02, 3.75) * mm});
            skLineSegment(sketch, "E404", {"start": v(38.02, 3.75) * mm, "end": v(37.2, 3.75) * mm});
            skLineSegment(sketch, "E405", {"start": v(37.2, 3.75) * mm, "end": v(36.39, 3.75) * mm});
            skLineSegment(sketch, "E406", {"start": v(36.39, 3.75) * mm, "end": v(36.39, 4.57) * mm});
            skLineSegment(sketch, "E407", {"start": v(36.39, 4.57) * mm, "end": v(37.2, 4.57) * mm});
            skLineSegment(sketch, "E408", {"start": v(37.2, 4.57) * mm, "end": v(37.2, 5.39) * mm});
            skLineSegment(sketch, "E409", {"start": v(37.2, 5.39) * mm, "end": v(36.39, 5.39) * mm});
            skLineSegment(sketch, "E410", {"start": v(36.39, 5.39) * mm, "end": v(36.39, 6.2) * mm});
            skLineSegment(sketch, "E411", {"start": v(36.39, 6.2) * mm, "end": v(35.57, 6.2) * mm});
            skLineSegment(sketch, "E412", {"start": v(35.57, 6.2) * mm, "end": v(35.57, 5.39) * mm});
            skLineSegment(sketch, "E413", {"start": v(35.57, 5.39) * mm, "end": v(34.76, 5.39) * mm});
            skLineSegment(sketch, "E414", {"start": v(34.76, 5.39) * mm, "end": v(34.76, 6.2) * mm});
            skLineSegment(sketch, "E415", {"start": v(34.76, 6.2) * mm, "end": v(34.76, 7.02) * mm});
            skLineSegment(sketch, "E416", {"start": v(34.76, 7.02) * mm, "end": v(34.76, 7.83) * mm});
            skLineSegment(sketch, "E417", {"start": v(34.76, 7.83) * mm, "end": v(35.57, 7.83) * mm});
            skLineSegment(sketch, "E418", {"start": v(35.57, 7.83) * mm, "end": v(36.39, 7.83) * mm});
            skLineSegment(sketch, "E419", {"start": v(36.39, 7.83) * mm, "end": v(36.39, 7.02) * mm});
            skLineSegment(sketch, "E420", {"start": v(36.39, 7.02) * mm, "end": v(37.2, 7.02) * mm});
            skLineSegment(sketch, "E421", {"start": v(37.2, 7.02) * mm, "end": v(37.2, 7.83) * mm});
            skLineSegment(sketch, "E422", {"start": v(37.2, 7.83) * mm, "end": v(38.02, 7.83) * mm});
            skLineSegment(sketch, "E423", {"start": v(38.02, 7.83) * mm, "end": v(38.02, 8.65) * mm});
            skLineSegment(sketch, "E424", {"start": v(38.02, 8.65) * mm, "end": v(38.02, 9.46) * mm});
            skLineSegment(sketch, "E425", {"start": v(38.02, 9.46) * mm, "end": v(38.02, 10.28) * mm});
            skLineSegment(sketch, "E426", {"start": v(38.02, 10.28) * mm, "end": v(38.02, 11.1) * mm});
            skLineSegment(sketch, "E427", {"start": v(38.02, 11.1) * mm, "end": v(37.2, 11.1) * mm});
            skLineSegment(sketch, "E428", {"start": v(29.86, 7.83) * mm, "end": v(29.86, 8.65) * mm});
            skLineSegment(sketch, "E429", {"start": v(29.86, 8.65) * mm, "end": v(29.86, 9.46) * mm});
            skLineSegment(sketch, "E430", {"start": v(29.86, 9.46) * mm, "end": v(29.05, 9.46) * mm});
            skLineSegment(sketch, "E431", {"start": v(29.05, 9.46) * mm, "end": v(29.05, 10.28) * mm});
            skLineSegment(sketch, "E432", {"start": v(29.05, 10.28) * mm, "end": v(28.23, 10.28) * mm});
            skLineSegment(sketch, "E433", {"start": v(28.23, 10.28) * mm, "end": v(27.42, 10.28) * mm});
            skLineSegment(sketch, "E434", {"start": v(27.42, 10.28) * mm, "end": v(26.6, 10.28) * mm});
            skLineSegment(sketch, "E435", {"start": v(26.6, 10.28) * mm, "end": v(26.6, 9.46) * mm});
            skLineSegment(sketch, "E436", {"start": v(26.6, 9.46) * mm, "end": v(25.78, 9.46) * mm});
            skLineSegment(sketch, "E437", {"start": v(25.78, 9.46) * mm, "end": v(25.78, 8.65) * mm});
            skLineSegment(sketch, "E438", {"start": v(25.78, 8.65) * mm, "end": v(25.78, 7.83) * mm});
            skLineSegment(sketch, "E439", {"start": v(25.78, 7.83) * mm, "end": v(24.97, 7.83) * mm});
            skLineSegment(sketch, "E440", {"start": v(24.97, 7.83) * mm, "end": v(24.97, 7.02) * mm});
            skLineSegment(sketch, "E441", {"start": v(24.97, 7.02) * mm, "end": v(25.78, 7.02) * mm});
            skLineSegment(sketch, "E442", {"start": v(25.78, 7.02) * mm, "end": v(26.6, 7.02) * mm});
            skLineSegment(sketch, "E443", {"start": v(26.6, 7.02) * mm, "end": v(27.42, 7.02) * mm});
            skLineSegment(sketch, "E444", {"start": v(27.42, 7.02) * mm, "end": v(28.23, 7.02) * mm});
            skLineSegment(sketch, "E445", {"start": v(28.23, 7.02) * mm, "end": v(28.23, 7.83) * mm});
            skLineSegment(sketch, "E446", {"start": v(28.23, 7.83) * mm, "end": v(27.42, 7.83) * mm});
            skLineSegment(sketch, "E447", {"start": v(27.42, 7.83) * mm, "end": v(26.6, 7.83) * mm});
            skLineSegment(sketch, "E448", {"start": v(26.6, 7.83) * mm, "end": v(26.6, 8.65) * mm});
            skLineSegment(sketch, "E449", {"start": v(26.6, 8.65) * mm, "end": v(27.42, 8.65) * mm});
            skLineSegment(sketch, "E450", {"start": v(27.42, 8.65) * mm, "end": v(28.23, 8.65) * mm});
            skLineSegment(sketch, "E451", {"start": v(28.23, 8.65) * mm, "end": v(28.23, 7.83) * mm});
            skLineSegment(sketch, "E452", {"start": v(28.23, 7.83) * mm, "end": v(29.05, 7.83) * mm});
            skLineSegment(sketch, "E453", {"start": v(29.05, 7.83) * mm, "end": v(29.86, 7.83) * mm});
            skLineSegment(sketch, "E454", {"start": v(25.78, 9.46) * mm, "end": v(25.78, 10.28) * mm});
            skLineSegment(sketch, "E455", {"start": v(25.78, 10.28) * mm, "end": v(26.6, 10.28) * mm});
            skLineSegment(sketch, "E456", {"start": v(26.6, 10.28) * mm, "end": v(26.6, 11.1) * mm});
            skLineSegment(sketch, "E457", {"start": v(26.6, 11.1) * mm, "end": v(26.6, 11.91) * mm});
            skLineSegment(sketch, "E458", {"start": v(26.6, 11.91) * mm, "end": v(25.78, 11.91) * mm});
            skLineSegment(sketch, "E459", {"start": v(25.78, 11.91) * mm, "end": v(25.78, 11.1) * mm});
            skLineSegment(sketch, "E460", {"start": v(25.78, 11.1) * mm, "end": v(24.97, 11.1) * mm});
            skLineSegment(sketch, "E461", {"start": v(24.97, 11.1) * mm, "end": v(24.97, 11.91) * mm});
            skLineSegment(sketch, "E462", {"start": v(24.97, 11.91) * mm, "end": v(25.78, 11.91) * mm});
            skLineSegment(sketch, "E463", {"start": v(25.78, 11.91) * mm, "end": v(25.78, 12.73) * mm});
            skLineSegment(sketch, "E464", {"start": v(25.78, 12.73) * mm, "end": v(25.78, 13.54) * mm});
            skLineSegment(sketch, "E465", {"start": v(25.78, 13.54) * mm, "end": v(24.97, 13.54) * mm});
            skLineSegment(sketch, "E466", {"start": v(24.97, 13.54) * mm, "end": v(24.97, 12.73) * mm});
            skLineSegment(sketch, "E467", {"start": v(24.97, 12.73) * mm, "end": v(24.15, 12.73) * mm});
            skLineSegment(sketch, "E468", {"start": v(24.15, 12.73) * mm, "end": v(24.15, 11.91) * mm});
            skLineSegment(sketch, "E469", {"start": v(24.15, 11.91) * mm, "end": v(23.34, 11.91) * mm});
            skLineSegment(sketch, "E470", {"start": v(23.34, 11.91) * mm, "end": v(22.52, 11.91) * mm});
            skLineSegment(sketch, "E471", {"start": v(22.52, 11.91) * mm, "end": v(21.7, 11.91) * mm});
            skLineSegment(sketch, "E472", {"start": v(21.7, 11.91) * mm, "end": v(21.7, 11.1) * mm});
            skLineSegment(sketch, "E473", {"start": v(21.7, 11.1) * mm, "end": v(22.52, 11.1) * mm});
            skLineSegment(sketch, "E474", {"start": v(22.52, 11.1) * mm, "end": v(23.34, 11.1) * mm});
            skLineSegment(sketch, "E475", {"start": v(23.34, 11.1) * mm, "end": v(24.15, 11.1) * mm});
            skLineSegment(sketch, "E476", {"start": v(24.15, 11.1) * mm, "end": v(24.15, 10.28) * mm});
            skLineSegment(sketch, "E477", {"start": v(24.15, 10.28) * mm, "end": v(24.97, 10.28) * mm});
            skLineSegment(sketch, "E478", {"start": v(24.97, 10.28) * mm, "end": v(24.97, 9.46) * mm});
            skLineSegment(sketch, "E479", {"start": v(24.97, 9.46) * mm, "end": v(25.78, 9.46) * mm});
            skLineSegment(sketch, "E480", {"start": v(24.97, 9.46) * mm, "end": v(24.15, 9.46) * mm});
            skLineSegment(sketch, "E481", {"start": v(24.15, 9.46) * mm, "end": v(24.15, 8.65) * mm});
            skLineSegment(sketch, "E482", {"start": v(24.15, 8.65) * mm, "end": v(24.97, 8.65) * mm});
            skLineSegment(sketch, "E483", {"start": v(24.97, 8.65) * mm, "end": v(24.97, 9.46) * mm});
            skLineSegment(sketch, "E484", {"start": v(24.15, 9.46) * mm, "end": v(24.15, 10.28) * mm});
            skLineSegment(sketch, "E485", {"start": v(24.15, 10.28) * mm, "end": v(23.34, 10.28) * mm});
            skLineSegment(sketch, "E486", {"start": v(23.34, 10.28) * mm, "end": v(22.52, 10.28) * mm});
            skLineSegment(sketch, "E487", {"start": v(22.52, 10.28) * mm, "end": v(21.7, 10.28) * mm});
            skLineSegment(sketch, "E488", {"start": v(21.7, 10.28) * mm, "end": v(20.9, 10.28) * mm});
            skLineSegment(sketch, "E489", {"start": v(20.9, 10.28) * mm, "end": v(20.9, 9.46) * mm});
            skLineSegment(sketch, "E490", {"start": v(20.9, 9.46) * mm, "end": v(21.7, 9.46) * mm});
            skLineSegment(sketch, "E491", {"start": v(21.7, 9.46) * mm, "end": v(22.52, 9.46) * mm});
            skLineSegment(sketch, "E492", {"start": v(22.52, 9.46) * mm, "end": v(23.34, 9.46) * mm});
            skLineSegment(sketch, "E493", {"start": v(23.34, 9.46) * mm, "end": v(24.15, 9.46) * mm});
            skLineSegment(sketch, "E494", {"start": v(20.9, 10.28) * mm, "end": v(20.9, 11.1) * mm});
            skLineSegment(sketch, "E495", {"start": v(20.9, 11.1) * mm, "end": v(20.07, 11.1) * mm});
            skLineSegment(sketch, "E496", {"start": v(20.07, 11.1) * mm, "end": v(19.26, 11.1) * mm});
            skLineSegment(sketch, "E497", {"start": v(19.26, 11.1) * mm, "end": v(19.26, 10.28) * mm});
            skLineSegment(sketch, "E498", {"start": v(19.26, 10.28) * mm, "end": v(20.07, 10.28) * mm});
            skLineSegment(sketch, "E499", {"start": v(20.07, 10.28) * mm, "end": v(20.9, 10.28) * mm});
            skLineSegment(sketch, "E500", {"start": v(19.26, 11.1) * mm, "end": v(19.26, 11.91) * mm});
            skLineSegment(sketch, "E501", {"start": v(19.26, 11.91) * mm, "end": v(18.44, 11.91) * mm});
            skLineSegment(sketch, "E502", {"start": v(18.44, 11.91) * mm, "end": v(18.44, 11.1) * mm});
            skLineSegment(sketch, "E503", {"start": v(18.44, 11.1) * mm, "end": v(19.26, 11.1) * mm});
            skLineSegment(sketch, "E504", {"start": v(18.44, 11.1) * mm, "end": v(17.63, 11.1) * mm});
            skLineSegment(sketch, "E505", {"start": v(17.63, 11.1) * mm, "end": v(17.63, 10.28) * mm});
            skLineSegment(sketch, "E506", {"start": v(17.63, 10.28) * mm, "end": v(18.44, 10.28) * mm});
            skLineSegment(sketch, "E507", {"start": v(18.44, 10.28) * mm, "end": v(18.44, 11.1) * mm});
            skLineSegment(sketch, "E508", {"start": v(19.26, 11.91) * mm, "end": v(20.07, 11.91) * mm});
            skLineSegment(sketch, "E509", {"start": v(20.07, 11.91) * mm, "end": v(20.07, 12.73) * mm});
            skLineSegment(sketch, "E510", {"start": v(20.07, 12.73) * mm, "end": v(20.9, 12.73) * mm});
            skLineSegment(sketch, "E511", {"start": v(20.9, 12.73) * mm, "end": v(21.7, 12.73) * mm});
            skLineSegment(sketch, "E512", {"start": v(21.7, 12.73) * mm, "end": v(21.7, 13.54) * mm});
            skLineSegment(sketch, "E513", {"start": v(21.7, 13.54) * mm, "end": v(21.7, 14.36) * mm});
            skLineSegment(sketch, "E514", {"start": v(21.7, 14.36) * mm, "end": v(20.9, 14.36) * mm});
            skLineSegment(sketch, "E515", {"start": v(20.9, 14.36) * mm, "end": v(20.9, 13.54) * mm});
            skLineSegment(sketch, "E516", {"start": v(20.9, 13.54) * mm, "end": v(20.07, 13.54) * mm});
            skLineSegment(sketch, "E517", {"start": v(20.07, 13.54) * mm, "end": v(19.26, 13.54) * mm});
            skLineSegment(sketch, "E518", {"start": v(19.26, 13.54) * mm, "end": v(19.26, 12.73) * mm});
            skLineSegment(sketch, "E519", {"start": v(19.26, 12.73) * mm, "end": v(19.26, 11.91) * mm});
            skLineSegment(sketch, "E520", {"start": v(21.7, 14.36) * mm, "end": v(22.52, 14.36) * mm});
            skLineSegment(sketch, "E521", {"start": v(22.52, 14.36) * mm, "end": v(23.34, 14.36) * mm});
            skLineSegment(sketch, "E522", {"start": v(23.34, 14.36) * mm, "end": v(23.34, 13.54) * mm});
            skLineSegment(sketch, "E523", {"start": v(23.34, 13.54) * mm, "end": v(24.15, 13.54) * mm});
            skLineSegment(sketch, "E524", {"start": v(24.15, 13.54) * mm, "end": v(24.97, 13.54) * mm});
            skLineSegment(sketch, "E525", {"start": v(24.97, 13.54) * mm, "end": v(24.97, 14.36) * mm});
            skLineSegment(sketch, "E526", {"start": v(24.97, 14.36) * mm, "end": v(24.15, 14.36) * mm});
            skLineSegment(sketch, "E527", {"start": v(24.15, 14.36) * mm, "end": v(24.15, 15.17) * mm});
            skLineSegment(sketch, "E528", {"start": v(24.15, 15.17) * mm, "end": v(23.34, 15.17) * mm});
            skLineSegment(sketch, "E529", {"start": v(23.34, 15.17) * mm, "end": v(22.52, 15.17) * mm});
            skLineSegment(sketch, "E530", {"start": v(22.52, 15.17) * mm, "end": v(21.7, 15.17) * mm});
            skLineSegment(sketch, "E531", {"start": v(21.7, 15.17) * mm, "end": v(21.7, 14.36) * mm});
            skLineSegment(sketch, "E532", {"start": v(23.34, 13.54) * mm, "end": v(22.52, 13.54) * mm});
            skLineSegment(sketch, "E533", {"start": v(22.52, 13.54) * mm, "end": v(22.52, 12.73) * mm});
            skLineSegment(sketch, "E534", {"start": v(22.52, 12.73) * mm, "end": v(23.34, 12.73) * mm});
            skLineSegment(sketch, "E535", {"start": v(23.34, 12.73) * mm, "end": v(23.34, 13.54) * mm});
            skLineSegment(sketch, "E536", {"start": v(29.05, 16.8) * mm, "end": v(29.05, 15.99) * mm});
            skLineSegment(sketch, "E537", {"start": v(29.05, 15.99) * mm, "end": v(29.05, 15.17) * mm});
            skLineSegment(sketch, "E538", {"start": v(29.05, 15.17) * mm, "end": v(29.86, 15.17) * mm});
            skLineSegment(sketch, "E539", {"start": v(29.86, 15.17) * mm, "end": v(29.86, 15.99) * mm});
            skLineSegment(sketch, "E540", {"start": v(29.86, 15.99) * mm, "end": v(29.86, 16.8) * mm});
            skLineSegment(sketch, "E541", {"start": v(29.86, 16.8) * mm, "end": v(29.05, 16.8) * mm});
            skLineSegment(sketch, "E542", {"start": v(31.5, 9.46) * mm, "end": v(32.3, 9.46) * mm});
            skLineSegment(sketch, "E543", {"start": v(32.3, 9.46) * mm, "end": v(33.12, 9.46) * mm});
            skLineSegment(sketch, "E544", {"start": v(33.12, 9.46) * mm, "end": v(33.94, 9.46) * mm});
            skLineSegment(sketch, "E545", {"start": v(33.94, 9.46) * mm, "end": v(33.94, 8.65) * mm});
            skLineSegment(sketch, "E546", {"start": v(33.94, 8.65) * mm, "end": v(33.94, 7.83) * mm});
            skLineSegment(sketch, "E547", {"start": v(33.94, 7.83) * mm, "end": v(33.94, 7.02) * mm});
            skLineSegment(sketch, "E548", {"start": v(33.94, 7.02) * mm, "end": v(33.12, 7.02) * mm});
            skLineSegment(sketch, "E549", {"start": v(33.12, 7.02) * mm, "end": v(32.3, 7.02) * mm});
            skLineSegment(sketch, "E550", {"start": v(32.3, 7.02) * mm, "end": v(31.5, 7.02) * mm});
            skLineSegment(sketch, "E551", {"start": v(31.5, 7.02) * mm, "end": v(31.5, 7.83) * mm});
            skLineSegment(sketch, "E552", {"start": v(31.5, 7.83) * mm, "end": v(31.5, 8.65) * mm});
            skLineSegment(sketch, "E553", {"start": v(31.5, 8.65) * mm, "end": v(31.5, 9.46) * mm});
            skLineSegment(sketch, "E554", {"start": v(34.76, 9.46) * mm, "end": v(35.57, 9.46) * mm});
            skLineSegment(sketch, "E555", {"start": v(35.57, 9.46) * mm, "end": v(36.39, 9.46) * mm});
            skLineSegment(sketch, "E556", {"start": v(36.39, 9.46) * mm, "end": v(37.2, 9.46) * mm});
            skLineSegment(sketch, "E557", {"start": v(37.2, 9.46) * mm, "end": v(37.2, 8.65) * mm});
            skLineSegment(sketch, "E558", {"start": v(37.2, 8.65) * mm, "end": v(36.39, 8.65) * mm});
            skLineSegment(sketch, "E559", {"start": v(36.39, 8.65) * mm, "end": v(35.57, 8.65) * mm});
            skLineSegment(sketch, "E560", {"start": v(35.57, 8.65) * mm, "end": v(34.76, 8.65) * mm});
            skLineSegment(sketch, "E561", {"start": v(34.76, 8.65) * mm, "end": v(34.76, 9.46) * mm});
            skLineSegment(sketch, "E562", {"start": v(17.63, 8.65) * mm, "end": v(17.63, 7.83) * mm});
            skLineSegment(sketch, "E563", {"start": v(17.63, 7.83) * mm, "end": v(17.63, 7.02) * mm});
            skLineSegment(sketch, "E564", {"start": v(17.63, 7.02) * mm, "end": v(17.63, 6.2) * mm});
            skLineSegment(sketch, "E565", {"start": v(17.63, 6.2) * mm, "end": v(17.63, 5.39) * mm});
            skLineSegment(sketch, "E566", {"start": v(17.63, 5.39) * mm, "end": v(17.63, 4.57) * mm});
            skLineSegment(sketch, "E567", {"start": v(17.63, 4.57) * mm, "end": v(17.63, 3.75) * mm});
            skLineSegment(sketch, "E568", {"start": v(17.63, 3.75) * mm, "end": v(17.63, 2.94) * mm});
            skLineSegment(sketch, "E569", {"start": v(17.63, 2.94) * mm, "end": v(18.44, 2.94) * mm});
            skLineSegment(sketch, "E570", {"start": v(18.44, 2.94) * mm, "end": v(19.26, 2.94) * mm});
            skLineSegment(sketch, "E571", {"start": v(19.26, 2.94) * mm, "end": v(20.07, 2.94) * mm});
            skLineSegment(sketch, "E572", {"start": v(20.07, 2.94) * mm, "end": v(20.9, 2.94) * mm});
            skLineSegment(sketch, "E573", {"start": v(20.9, 2.94) * mm, "end": v(21.7, 2.94) * mm});
            skLineSegment(sketch, "E574", {"start": v(21.7, 2.94) * mm, "end": v(22.52, 2.94) * mm});
            skLineSegment(sketch, "E575", {"start": v(22.52, 2.94) * mm, "end": v(23.34, 2.94) * mm});
            skLineSegment(sketch, "E576", {"start": v(23.34, 2.94) * mm, "end": v(23.34, 3.75) * mm});
            skLineSegment(sketch, "E577", {"start": v(23.34, 3.75) * mm, "end": v(23.34, 4.57) * mm});
            skLineSegment(sketch, "E578", {"start": v(23.34, 4.57) * mm, "end": v(23.34, 5.39) * mm});
            skLineSegment(sketch, "E579", {"start": v(23.34, 5.39) * mm, "end": v(23.34, 6.2) * mm});
            skLineSegment(sketch, "E580", {"start": v(23.34, 6.2) * mm, "end": v(23.34, 7.02) * mm});
            skLineSegment(sketch, "E581", {"start": v(23.34, 7.02) * mm, "end": v(23.34, 7.83) * mm});
            skLineSegment(sketch, "E582", {"start": v(23.34, 7.83) * mm, "end": v(23.34, 8.65) * mm});
            skLineSegment(sketch, "E583", {"start": v(23.34, 8.65) * mm, "end": v(22.52, 8.65) * mm});
            skLineSegment(sketch, "E584", {"start": v(22.52, 8.65) * mm, "end": v(21.7, 8.65) * mm});
            skLineSegment(sketch, "E585", {"start": v(21.7, 8.65) * mm, "end": v(20.9, 8.65) * mm});
            skLineSegment(sketch, "E586", {"start": v(20.9, 8.65) * mm, "end": v(20.07, 8.65) * mm});
            skLineSegment(sketch, "E587", {"start": v(20.07, 8.65) * mm, "end": v(19.26, 8.65) * mm});
            skLineSegment(sketch, "E588", {"start": v(19.26, 8.65) * mm, "end": v(18.44, 8.65) * mm});
            skLineSegment(sketch, "E589", {"start": v(18.44, 8.65) * mm, "end": v(17.63, 8.65) * mm});
            skLineSegment(sketch, "E590", {"start": v(32.3, 8.65) * mm, "end": v(32.3, 7.83) * mm});
            skLineSegment(sketch, "E591", {"start": v(32.3, 7.83) * mm, "end": v(33.12, 7.83) * mm});
            skLineSegment(sketch, "E592", {"start": v(33.12, 7.83) * mm, "end": v(33.12, 8.65) * mm});
            skLineSegment(sketch, "E593", {"start": v(33.12, 8.65) * mm, "end": v(32.3, 8.65) * mm});
            skLineSegment(sketch, "E594", {"start": v(18.44, 7.83) * mm, "end": v(19.26, 7.83) * mm});
            skLineSegment(sketch, "E595", {"start": v(19.26, 7.83) * mm, "end": v(20.07, 7.83) * mm});
            skLineSegment(sketch, "E596", {"start": v(20.07, 7.83) * mm, "end": v(20.9, 7.83) * mm});
            skLineSegment(sketch, "E597", {"start": v(20.9, 7.83) * mm, "end": v(21.7, 7.83) * mm});
            skLineSegment(sketch, "E598", {"start": v(21.7, 7.83) * mm, "end": v(22.52, 7.83) * mm});
            skLineSegment(sketch, "E599", {"start": v(22.52, 7.83) * mm, "end": v(22.52, 7.02) * mm});
            skLineSegment(sketch, "E600", {"start": v(22.52, 7.02) * mm, "end": v(22.52, 6.2) * mm});
            skLineSegment(sketch, "E601", {"start": v(22.52, 6.2) * mm, "end": v(22.52, 5.39) * mm});
            skLineSegment(sketch, "E602", {"start": v(22.52, 5.39) * mm, "end": v(22.52, 4.57) * mm});
            skLineSegment(sketch, "E603", {"start": v(22.52, 4.57) * mm, "end": v(22.52, 3.75) * mm});
            skLineSegment(sketch, "E604", {"start": v(22.52, 3.75) * mm, "end": v(21.7, 3.75) * mm});
            skLineSegment(sketch, "E605", {"start": v(21.7, 3.75) * mm, "end": v(20.9, 3.75) * mm});
            skLineSegment(sketch, "E606", {"start": v(20.9, 3.75) * mm, "end": v(20.07, 3.75) * mm});
            skLineSegment(sketch, "E607", {"start": v(20.07, 3.75) * mm, "end": v(19.26, 3.75) * mm});
            skLineSegment(sketch, "E608", {"start": v(19.26, 3.75) * mm, "end": v(18.44, 3.75) * mm});
            skLineSegment(sketch, "E609", {"start": v(18.44, 3.75) * mm, "end": v(18.44, 4.57) * mm});
            skLineSegment(sketch, "E610", {"start": v(18.44, 4.57) * mm, "end": v(18.44, 5.39) * mm});
            skLineSegment(sketch, "E611", {"start": v(18.44, 5.39) * mm, "end": v(18.44, 6.2) * mm});
            skLineSegment(sketch, "E612", {"start": v(18.44, 6.2) * mm, "end": v(18.44, 7.02) * mm});
            skLineSegment(sketch, "E613", {"start": v(18.44, 7.02) * mm, "end": v(18.44, 7.83) * mm});
            skLineSegment(sketch, "E614", {"start": v(19.26, 7.02) * mm, "end": v(19.26, 6.2) * mm});
            skLineSegment(sketch, "E615", {"start": v(19.26, 6.2) * mm, "end": v(19.26, 5.39) * mm});
            skLineSegment(sketch, "E616", {"start": v(19.26, 5.39) * mm, "end": v(19.26, 4.57) * mm});
            skLineSegment(sketch, "E617", {"start": v(19.26, 4.57) * mm, "end": v(20.07, 4.57) * mm});
            skLineSegment(sketch, "E618", {"start": v(20.07, 4.57) * mm, "end": v(20.9, 4.57) * mm});
            skLineSegment(sketch, "E619", {"start": v(20.9, 4.57) * mm, "end": v(21.7, 4.57) * mm});
            skLineSegment(sketch, "E620", {"start": v(21.7, 4.57) * mm, "end": v(21.7, 5.39) * mm});
            skLineSegment(sketch, "E621", {"start": v(21.7, 5.39) * mm, "end": v(21.7, 6.2) * mm});
            skLineSegment(sketch, "E622", {"start": v(21.7, 6.2) * mm, "end": v(21.7, 7.02) * mm});
            skLineSegment(sketch, "E623", {"start": v(21.7, 7.02) * mm, "end": v(20.9, 7.02) * mm});
            skLineSegment(sketch, "E624", {"start": v(20.9, 7.02) * mm, "end": v(20.07, 7.02) * mm});
            skLineSegment(sketch, "E625", {"start": v(20.07, 7.02) * mm, "end": v(19.26, 7.02) * mm});
            skLineSegment(sketch, "E626", {"start": v(24.15, 6.2) * mm, "end": v(24.15, 5.39) * mm});
            skLineSegment(sketch, "E627", {"start": v(24.15, 5.39) * mm, "end": v(24.15, 4.57) * mm});
            skLineSegment(sketch, "E628", {"start": v(24.15, 4.57) * mm, "end": v(24.15, 3.75) * mm});
            skLineSegment(sketch, "E629", {"start": v(24.15, 3.75) * mm, "end": v(24.15, 2.94) * mm});
            skLineSegment(sketch, "E630", {"start": v(24.15, 2.94) * mm, "end": v(24.97, 2.94) * mm});
            skLineSegment(sketch, "E631", {"start": v(24.97, 2.94) * mm, "end": v(25.78, 2.94) * mm});
            skLineSegment(sketch, "E632", {"start": v(25.78, 2.94) * mm, "end": v(25.78, 3.75) * mm});
            skLineSegment(sketch, "E633", {"start": v(25.78, 3.75) * mm, "end": v(24.97, 3.75) * mm});
            skLineSegment(sketch, "E634", {"start": v(24.97, 3.75) * mm, "end": v(24.97, 4.57) * mm});
            skLineSegment(sketch, "E635", {"start": v(24.97, 4.57) * mm, "end": v(25.78, 4.57) * mm});
            skLineSegment(sketch, "E636", {"start": v(25.78, 4.57) * mm, "end": v(25.78, 3.75) * mm});
            skLineSegment(sketch, "E637", {"start": v(25.78, 3.75) * mm, "end": v(26.6, 3.75) * mm});
            skLineSegment(sketch, "E638", {"start": v(26.6, 3.75) * mm, "end": v(26.6, 2.94) * mm});
            skLineSegment(sketch, "E639", {"start": v(26.6, 2.94) * mm, "end": v(27.42, 2.94) * mm});
            skLineSegment(sketch, "E640", {"start": v(27.42, 2.94) * mm, "end": v(28.23, 2.94) * mm});
            skLineSegment(sketch, "E641", {"start": v(28.23, 2.94) * mm, "end": v(29.05, 2.94) * mm});
            skLineSegment(sketch, "E642", {"start": v(29.05, 2.94) * mm, "end": v(29.86, 2.94) * mm});
            skLineSegment(sketch, "E643", {"start": v(29.86, 2.94) * mm, "end": v(29.86, 3.75) * mm});
            skLineSegment(sketch, "E644", {"start": v(29.86, 3.75) * mm, "end": v(29.05, 3.75) * mm});
            skLineSegment(sketch, "E645", {"start": v(29.05, 3.75) * mm, "end": v(29.05, 4.57) * mm});
            skLineSegment(sketch, "E646", {"start": v(29.05, 4.57) * mm, "end": v(29.05, 5.39) * mm});
            skLineSegment(sketch, "E647", {"start": v(29.05, 5.39) * mm, "end": v(29.05, 6.2) * mm});
            skLineSegment(sketch, "E648", {"start": v(29.05, 6.2) * mm, "end": v(28.23, 6.2) * mm});
            skLineSegment(sketch, "E649", {"start": v(28.23, 6.2) * mm, "end": v(28.23, 5.39) * mm});
            skLineSegment(sketch, "E650", {"start": v(28.23, 5.39) * mm, "end": v(28.23, 4.57) * mm});
            skLineSegment(sketch, "E651", {"start": v(28.23, 4.57) * mm, "end": v(27.42, 4.57) * mm});
            skLineSegment(sketch, "E652", {"start": v(27.42, 4.57) * mm, "end": v(27.42, 5.39) * mm});
            skLineSegment(sketch, "E653", {"start": v(27.42, 5.39) * mm, "end": v(27.42, 6.2) * mm});
            skLineSegment(sketch, "E654", {"start": v(27.42, 6.2) * mm, "end": v(26.6, 6.2) * mm});
            skLineSegment(sketch, "E655", {"start": v(26.6, 6.2) * mm, "end": v(26.6, 5.39) * mm});
            skLineSegment(sketch, "E656", {"start": v(26.6, 5.39) * mm, "end": v(25.78, 5.39) * mm});
            skLineSegment(sketch, "E657", {"start": v(25.78, 5.39) * mm, "end": v(24.97, 5.39) * mm});
            skLineSegment(sketch, "E658", {"start": v(24.97, 5.39) * mm, "end": v(24.97, 6.2) * mm});
            skLineSegment(sketch, "E659", {"start": v(24.97, 6.2) * mm, "end": v(24.15, 6.2) * mm});
            skLineSegment(sketch, "E660", {"start": v(29.86, 3.75) * mm, "end": v(30.68, 3.75) * mm});
            skLineSegment(sketch, "E661", {"start": v(30.68, 3.75) * mm, "end": v(30.68, 4.57) * mm});
            skLineSegment(sketch, "E662", {"start": v(30.68, 4.57) * mm, "end": v(29.86, 4.57) * mm});
            skLineSegment(sketch, "E663", {"start": v(29.86, 4.57) * mm, "end": v(29.86, 3.75) * mm});
            skLineSegment(sketch, "E664", {"start": v(34.76, 4.57) * mm, "end": v(35.57, 4.57) * mm});
            skLineSegment(sketch, "E665", {"start": v(35.57, 4.57) * mm, "end": v(35.57, 3.75) * mm});
            skLineSegment(sketch, "E666", {"start": v(35.57, 3.75) * mm, "end": v(34.76, 3.75) * mm});
            skLineSegment(sketch, "E667", {"start": v(34.76, 3.75) * mm, "end": v(34.76, 4.57) * mm});
            skLineSegment(sketch, "E668", {"start": v(24.15, 11.1) * mm, "end": v(24.97, 11.1) * mm});
            skLineSegment(sketch, "E669", {"start": v(24.15, 11.91) * mm, "end": v(24.97, 11.91) * mm});
            skLineSegment(sketch, "E670", {"start": v(24.97, 12.73) * mm, "end": v(24.97, 11.91) * mm});
            skLineSegment(sketch, "E671", {"start": v(24.97, 12.73) * mm, "end": v(25.78, 12.73) * mm});
            skLineSegment(sketch, "E672", {"start": v(25.78, 12.73) * mm, "end": v(24.97, 12.73) * mm});
            skLineSegment(sketch, "E673", {"start": v(29.05, 13.54) * mm, "end": v(29.05, 12.73) * mm});
            skLineSegment(sketch, "E674", {"start": v(32.3, 13.54) * mm, "end": v(33.12, 13.54) * mm});
            skLineSegment(sketch, "E675", {"start": v(29.86, 12.73) * mm, "end": v(29.86, 11.91) * mm});
            skLineSegment(sketch, "E676", {"start": v(32.3, 12.73) * mm, "end": v(32.3, 11.91) * mm});
            skLineSegment(sketch, "E677", {"start": v(32.3, 11.91) * mm, "end": v(33.12, 11.91) * mm});
            skSolve(sketch);
        }
        {
            var Q0;
            Q0=makeQuery(id+"F2.imprint","IMPRINT",FACE,{"disambiguationData":[TD([[makeQuery(id+"F2.imprint","IMPRINT",EDGE,{"derivedFrom":sQuery(id+"F2.wireOp",EDGE,"E192")}),1.0]])]});
            var Q1;
            Q1=makeQuery(id+"F2.imprint","IMPRINT",FACE,{"disambiguationData":[TD([[makeQuery(id+"F2.imprint","IMPRINT",EDGE,{"derivedFrom":sQuery(id+"F2.wireOp",EDGE,"E22")}),1.0]])]});
            var Q2;
            Q2=makeQuery(id+"F2.imprint","IMPRINT",FACE,{"disambiguationData":[TD([[makeQuery(id+"F2.imprint","IMPRINT",EDGE,{"derivedFrom":sQuery(id+"F2.wireOp",EDGE,"E50")}),1.0]])]});
            var Q3;
            Q3=makeQuery(id+"F2.imprint","IMPRINT",FACE,{"disambiguationData":[TD([[makeQuery(id+"F2.imprint","IMPRINT",EDGE,{"derivedFrom":sQuery(id+"F2.wireOp",EDGE,"E56")}),1.0]])]});
            var Q4;
            Q4=makeQuery(id+"F2.imprint","IMPRINT",FACE,{"disambiguationData":[TD([[makeQuery(id+"F2.imprint","IMPRINT",EDGE,{"derivedFrom":sQuery(id+"F2.wireOp",EDGE,"E120")}),1.0]])]});
            var Q5;
            Q5=makeQuery(id+"F2.imprint","IMPRINT",FACE,{"disambiguationData":[TD([[makeQuery(id+"F2.imprint","IMPRINT",EDGE,{"derivedFrom":sQuery(id+"F2.wireOp",EDGE,"E66")}),1.0]])]});
            var Q6;
            Q6=makeQuery(id+"F2.imprint","IMPRINT",FACE,{"disambiguationData":[TD([[makeQuery(id+"F2.imprint","IMPRINT",EDGE,{"derivedFrom":sQuery(id+"F2.wireOp",EDGE,"E96")}),1.0]])]});
            var Q7;
            Q7=makeQuery(id+"F2.imprint","IMPRINT",FACE,{"disambiguationData":[TD([[makeQuery(id+"F2.imprint","IMPRINT",EDGE,{"derivedFrom":sQuery(id+"F2.wireOp",EDGE,"E100")}),1.0]])]});
            var Q8;
            Q8=makeQuery(id+"F2.imprint","IMPRINT",FACE,{"disambiguationData":[TD([[makeQuery(id+"F2.imprint","IMPRINT",EDGE,{"derivedFrom":sQuery(id+"F2.wireOp",EDGE,"E112")}),1.0]])]});
            var Q9;
            Q9=makeQuery(id+"F2.imprint","IMPRINT",FACE,{"disambiguationData":[TD([[makeQuery(id+"F2.imprint","IMPRINT",EDGE,{"derivedFrom":sQuery(id+"F2.wireOp",EDGE,"E116")}),1.0]])]});
            var Q10;
            Q10=makeQuery(id+"F2.imprint","IMPRINT",FACE,{"disambiguationData":[TD([[makeQuery(id+"F2.imprint","IMPRINT",EDGE,{"derivedFrom":sQuery(id+"F2.wireOp",EDGE,"E232")}),1.0]])]});
            var Q11;
            Q11=makeQuery(id+"F2.imprint","IMPRINT",FACE,{"disambiguationData":[TD([[makeQuery(id+"F2.imprint","IMPRINT",EDGE,{"derivedFrom":sQuery(id+"F2.wireOp",EDGE,"E246")}),1.0]])]});
            var Q12;
            Q12=makeQuery(id+"F2.imprint","IMPRINT",FACE,{"disambiguationData":[TD([[makeQuery(id+"F2.imprint","IMPRINT",EDGE,{"derivedFrom":sQuery(id+"F2.wireOp",EDGE,"E504")}),1.0]])]});
            var Q13;
            Q13=makeQuery(id+"F2.imprint","IMPRINT",FACE,{"disambiguationData":[TD([[makeQuery(id+"F2.imprint","IMPRINT",EDGE,{"derivedFrom":sQuery(id+"F2.wireOp",EDGE,"E480")}),1.0]])]});
            var Q14;
            Q14=makeQuery(id+"F2.imprint","IMPRINT",FACE,{"disambiguationData":[TD([[makeQuery(id+"F2.imprint","IMPRINT",EDGE,{"derivedFrom":sQuery(id+"F2.wireOp",EDGE,"E494")}),1.0]])]});
            var Q15;
            Q15=makeQuery(id+"F2.imprint","IMPRINT",FACE,{"disambiguationData":[TD([[makeQuery(id+"F2.imprint","IMPRINT",EDGE,{"derivedFrom":sQuery(id+"F2.wireOp",EDGE,"E500")}),1.0]])]});
            var Q16;
            Q16=makeQuery(id+"F2.imprint","IMPRINT",FACE,{"disambiguationData":[TD([[makeQuery(id+"F2.imprint","IMPRINT",EDGE,{"derivedFrom":sQuery(id+"F2.wireOp",EDGE,"E508")}),1.0]])]});
            var Q17;
            Q17=makeQuery(id+"F2.imprint","IMPRINT",FACE,{"disambiguationData":[TD([[makeQuery(id+"F2.imprint","IMPRINT",EDGE,{"derivedFrom":sQuery(id+"F2.wireOp",EDGE,"E532")}),1.0]])]});
            var Q18;
            Q18=makeQuery(id+"F2.imprint","IMPRINT",FACE,{"disambiguationData":[TD([[makeQuery(id+"F2.imprint","IMPRINT",EDGE,{"derivedFrom":sQuery(id+"F2.wireOp",EDGE,"E484")}),1.0]])]});
            var Q19;
            Q19=makeQuery(id+"F2.imprint","IMPRINT",FACE,{"disambiguationData":[TD([[makeQuery(id+"F2.imprint","IMPRINT",EDGE,{"derivedFrom":sQuery(id+"F2.wireOp",EDGE,"E520")}),1.0]])]});
            var Q20;
            Q20=makeQuery(id+"F2.imprint","IMPRINT",FACE,{"disambiguationData":[TD([[makeQuery(id+"F2.imprint","IMPRINT",EDGE,{"derivedFrom":sQuery(id+"F2.wireOp",EDGE,"E454")}),1.0]])]});
            var Q21;
            Q21=makeQuery(id+"F2.imprint","IMPRINT",FACE,{"disambiguationData":[TD([[makeQuery(id+"F2.imprint","IMPRINT",EDGE,{"derivedFrom":sQuery(id+"F2.wireOp",EDGE,"E461")}),1.0]])]});
            var Q22;
            Q22=makeQuery(id+"F2.imprint","IMPRINT",FACE,{"disambiguationData":[TD([[makeQuery(id+"F2.imprint","IMPRINT",EDGE,{"derivedFrom":sQuery(id+"F2.wireOp",EDGE,"E467")}),1.0]])]});
            var Q23;
            Q23=makeQuery(id+"F2.imprint","IMPRINT",FACE,{"disambiguationData":[TD([[makeQuery(id+"F2.imprint","IMPRINT",EDGE,{"derivedFrom":sQuery(id+"F2.wireOp",EDGE,"E464")}),1.0]])]});
            var Q24;
            Q24=makeQuery(id+"F2.imprint","IMPRINT",FACE,{"disambiguationData":[TD([[makeQuery(id+"F2.imprint","IMPRINT",EDGE,{"derivedFrom":sQuery(id+"F2.wireOp",EDGE,"E260")}),1.0]])]});
            var Q25;
            Q25=makeQuery(id+"F2.imprint","IMPRINT",FACE,{"disambiguationData":[TD([[makeQuery(id+"F2.imprint","IMPRINT",EDGE,{"derivedFrom":sQuery(id+"F2.wireOp",EDGE,"E216")}),1.0]])]});
            var Q26;
            Q26=makeQuery(id+"F2.imprint","IMPRINT",FACE,{"disambiguationData":[TD([[makeQuery(id+"F2.imprint","IMPRINT",EDGE,{"derivedFrom":sQuery(id+"F2.wireOp",EDGE,"E220")}),1.0]])]});
            var Q27;
            Q27=makeQuery(id+"F2.imprint","IMPRINT",FACE,{"disambiguationData":[TD([[makeQuery(id+"F2.imprint","IMPRINT",EDGE,{"derivedFrom":sQuery(id+"F2.wireOp",EDGE,"E314")}),1.0]])]});
            var Q28;
            Q28=makeQuery(id+"F2.imprint","IMPRINT",FACE,{"disambiguationData":[TD([[makeQuery(id+"F2.imprint","IMPRINT",EDGE,{"derivedFrom":sQuery(id+"F2.wireOp",EDGE,"E318")}),1.0]])]});
            var Q29;
            Q29=makeQuery(id+"F2.imprint","IMPRINT",FACE,{"disambiguationData":[TD([[makeQuery(id+"F2.imprint","IMPRINT",EDGE,{"derivedFrom":sQuery(id+"F2.wireOp",EDGE,"E324")}),1.0]])]});
            var Q30;
            Q30=makeQuery(id+"F2.imprint","IMPRINT",FACE,{"disambiguationData":[TD([[makeQuery(id+"F2.imprint","IMPRINT",EDGE,{"derivedFrom":sQuery(id+"F2.wireOp",EDGE,"E332")}),1.0]])]});
            var Q31;
            Q31=makeQuery(id+"F2.imprint","IMPRINT",FACE,{"disambiguationData":[TD([[makeQuery(id+"F2.imprint","IMPRINT",EDGE,{"derivedFrom":sQuery(id+"F2.wireOp",EDGE,"E336")}),1.0]])]});
            var Q32;
            Q32=makeQuery(id+"F2.imprint","IMPRINT",FACE,{"disambiguationData":[TD([[makeQuery(id+"F2.imprint","IMPRINT",EDGE,{"derivedFrom":sQuery(id+"F2.wireOp",EDGE,"E536")}),1.0]])]});
            var Q33;
            Q33=makeQuery(id+"F2.imprint","IMPRINT",FACE,{"disambiguationData":[TD([[makeQuery(id+"F2.imprint","IMPRINT",EDGE,{"derivedFrom":sQuery(id+"F2.wireOp",EDGE,"E250")}),1.0]])]});
            var Q34;
            Q34=makeQuery(id+"F2.imprint","IMPRINT",FACE,{"disambiguationData":[TD([[makeQuery(id+"F2.imprint","IMPRINT",EDGE,{"derivedFrom":sQuery(id+"F2.wireOp",EDGE,"E271")}),1.0]])]});
            var Q35;
            Q35=makeQuery(id+"F2.imprint","IMPRINT",FACE,{"disambiguationData":[TD([[makeQuery(id+"F2.imprint","IMPRINT",EDGE,{"derivedFrom":sQuery(id+"F2.wireOp",EDGE,"E293")}),1.0]])]});
            var Q36;
            Q36=makeQuery(id+"F2.imprint","IMPRINT",FACE,{"disambiguationData":[TD([[makeQuery(id+"F2.imprint","IMPRINT",EDGE,{"derivedFrom":sQuery(id+"F2.wireOp",EDGE,"E279")}),1.0]])]});
            var Q37;
            Q37=makeQuery(id+"F2.imprint","IMPRINT",FACE,{"disambiguationData":[TD([[makeQuery(id+"F2.imprint","IMPRINT",EDGE,{"derivedFrom":sQuery(id+"F2.wireOp",EDGE,"E340")}),1.0]])]});
            var Q38;
            Q38=makeQuery(id+"F2.imprint","IMPRINT",FACE,{"disambiguationData":[TD([[makeQuery(id+"F2.imprint","IMPRINT",EDGE,{"derivedFrom":sQuery(id+"F2.wireOp",EDGE,"E660")}),1.0]])]});
            var Q39;
            Q39=makeQuery(id+"F2.imprint","IMPRINT",FACE,{"disambiguationData":[TD([[makeQuery(id+"F2.imprint","IMPRINT",EDGE,{"derivedFrom":sQuery(id+"F2.wireOp",EDGE,"E590")}),1.0]])]});
            var Q40;
            Q40=makeQuery(id+"F2.imprint","IMPRINT",FACE,{"disambiguationData":[TD([[makeQuery(id+"F2.imprint","IMPRINT",EDGE,{"derivedFrom":sQuery(id+"F2.wireOp",EDGE,"E354")}),1.0]])]});
            extrude(context, id + "F3", {"entities" : qUnion([Q0, Q1, Q2, Q3, Q4, Q5, Q6, Q7, Q8, Q9, Q10, Q11, Q12, Q13, Q14, Q15, Q16, Q17, Q18, Q19, Q20, Q21, Q22, Q23, Q24, Q25, Q26, Q27, Q28, Q29, Q30, Q31, Q32, Q33, Q34, Q35, Q36, Q37, Q38, Q39, Q40]), "depth" : 0.5 * mm});
        }
        {
            var Q0;
            Q0=makeQuery(id+"F2.imprint","IMPRINT",FACE,{"disambiguationData":[TD([[makeQuery(id+"F2.imprint","IMPRINT",EDGE,{"derivedFrom":sQuery(id+"F2.wireOp",EDGE,"E463")}),1.0]])]});
            var Q1;
            Q1=makeQuery(id+"F2.imprint","IMPRINT",FACE,{"disambiguationData":[TD([[makeQuery(id+"F2.imprint","IMPRINT",EDGE,{"derivedFrom":sQuery(id+"F2.wireOp",EDGE,"E285")}),1.0]])]});
            extrude(context, id + "F4", {"entities" : qUnion([Q0, Q1]), "depth" : 0.5 * mm});
        }
    });
